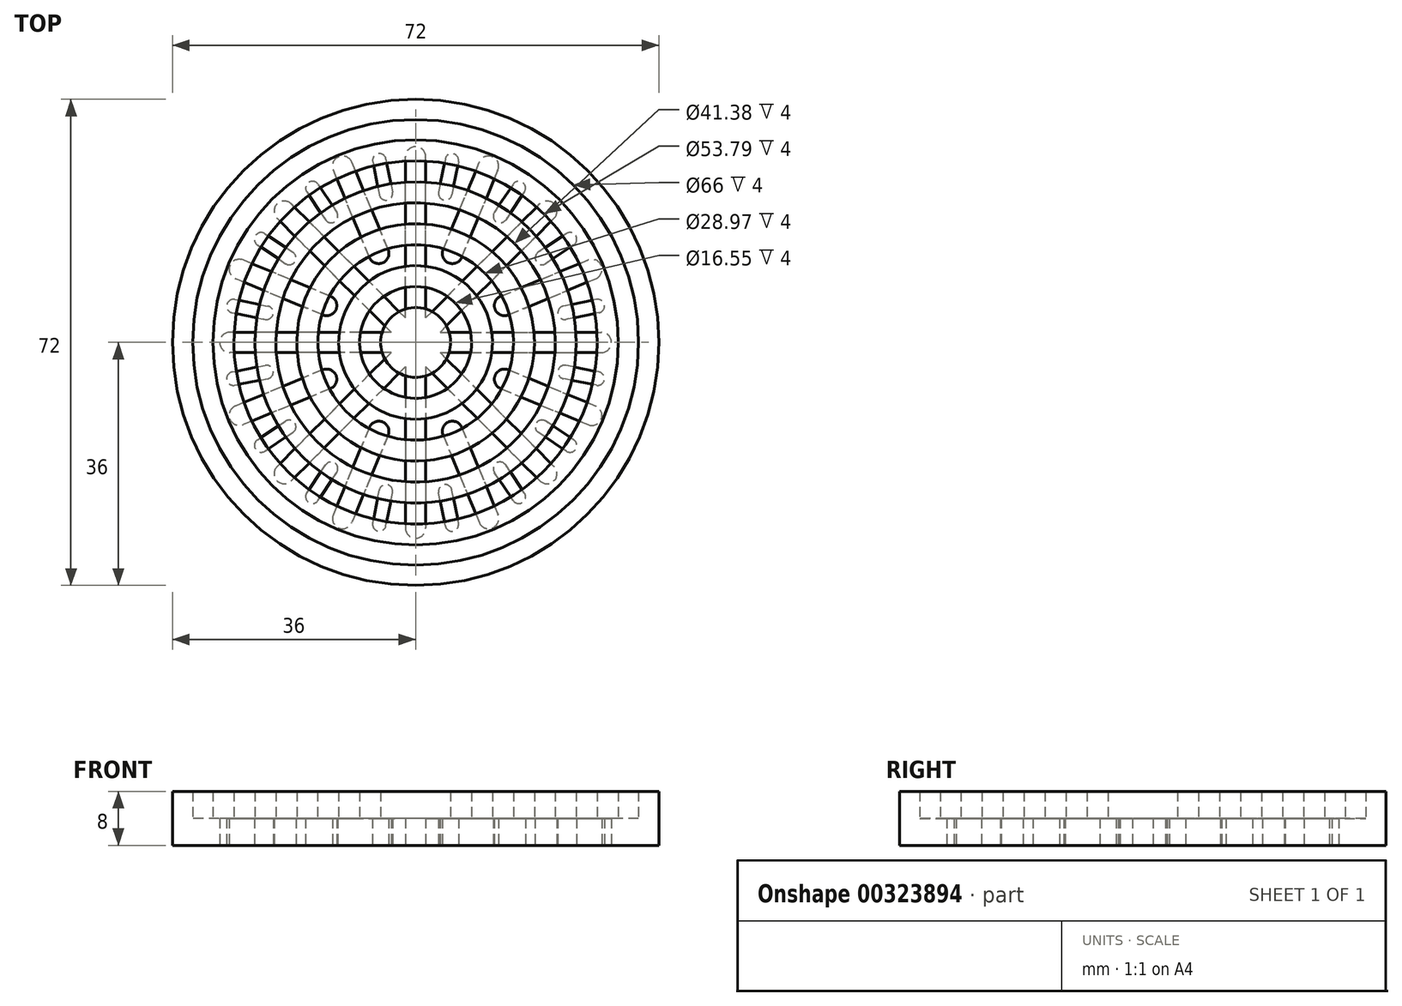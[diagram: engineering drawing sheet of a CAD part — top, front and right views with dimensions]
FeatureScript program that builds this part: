
annotation { "Feature Type Name" : "Feature", "Feature Type Description" : "" }
export const myFeature = defineFeature(function(context is Context, id is Id, definition is map)
    precondition{}
    {
        {
            var Q0;
            Q0=qCreatedBy(makeId("Top.planeOp"),FACE);
            var sketch = newSketch(context, id + "F0", { "sketchPlane" : qUnion([Q0])});
            skCircle(sketch, "E0", {"center": v(0, 0) * mm, "radius": 36 * mm});
            skArc(sketch, "E1.0.endCap", {"start": v(-1.5, 27.5) * mm, "mid": v(0, 29) * mm, "end": v(1.5, 27.5) * mm});
            skArc(sketch, "E2.0.startCap", {"start": v(6.84, 12.6) * mm, "mid": v(4.88, 11.78) * mm, "end": v(4.07, 13.74) * mm});
            skArc(sketch, "E2.0.endCap", {"start": v(9.42, 26.67) * mm, "mid": v(11.38, 27.49) * mm, "end": v(12.2, 25.53) * mm});
            skLineSegment(sketch, "E2.0.left", {"start": v(4.07, 13.74) * mm, "end": v(9.42, 26.67) * mm});
            skLineSegment(sketch, "E2.0.right", {"start": v(6.84, 12.6) * mm, "end": v(12.2, 25.53) * mm});
            skArc(sketch, "E3.0.startCap", {"start": v(4.38, 27.17) * mm, "mid": v(5.56, 27.95) * mm, "end": v(6.35, 26.78) * mm});
            skArc(sketch, "E3.0.endCap", {"start": v(5.37, 21.87) * mm, "mid": v(4.2, 21.09) * mm, "end": v(3.4, 22.26) * mm});
            skLineSegment(sketch, "E3.0.left", {"start": v(6.35, 26.78) * mm, "end": v(5.37, 21.87) * mm});
            skLineSegment(sketch, "E3.0.right", {"start": v(4.38, 27.17) * mm, "end": v(3.4, 22.26) * mm});
            skArc(sketch, "E4.1.0", {"start": v(-20.5, 18.38) * mm, "mid": v(-20.5, 20.5) * mm, "end": v(-18.38, 20.5) * mm});
            skArc(sketch, "E4.2.0", {"start": v(-27.5, -1.5) * mm, "mid": v(-29, 0) * mm, "end": v(-27.5, 1.5) * mm});
            skArc(sketch, "E4.3.0", {"start": v(-18.38, -20.5) * mm, "mid": v(-20.5, -20.5) * mm, "end": v(-20.5, -18.38) * mm});
            skArc(sketch, "E4.4.0", {"start": v(1.5, -27.5) * mm, "mid": v(0, -29) * mm, "end": v(-1.5, -27.5) * mm});
            skArc(sketch, "E4.5.0", {"start": v(20.5, -18.38) * mm, "mid": v(20.5, -20.5) * mm, "end": v(18.38, -20.5) * mm});
            skArc(sketch, "E4.6.0", {"start": v(27.5, 1.5) * mm, "mid": v(29, 0) * mm, "end": v(27.5, -1.5) * mm});
            skArc(sketch, "E4.7.0", {"start": v(18.38, 20.5) * mm, "mid": v(20.5, 20.5) * mm, "end": v(20.5, 18.38) * mm});
            skLineSegment(sketch, "E5.trimOffspring", {"start": v(-1.5, 3.62) * mm, "end": v(-1.5, 27.5) * mm});
            skLineSegment(sketch, "E6.trimOffspring", {"start": v(-3.62, 1.5) * mm, "end": v(-27.5, 1.5) * mm});
            skLineSegment(sketch, "E7.trimOffspring", {"start": v(-1.5, 3.62) * mm, "end": v(-18.38, 20.5) * mm});
            skLineSegment(sketch, "E8.trimOffspring", {"start": v(1.5, 3.62) * mm, "end": v(18.38, 20.5) * mm});
            skLineSegment(sketch, "E9.trimOffspring", {"start": v(1.5, 3.62) * mm, "end": v(1.5, 27.5) * mm});
            skLineSegment(sketch, "E10.trimOffspring", {"start": v(3.62, 1.5) * mm, "end": v(27.5, 1.5) * mm});
            skLineSegment(sketch, "E11.trimOffspring", {"start": v(3.62, 1.5) * mm, "end": v(20.5, 18.38) * mm});
            skLineSegment(sketch, "E12.trimOffspring", {"start": v(3.62, -1.5) * mm, "end": v(20.5, -18.38) * mm});
            skLineSegment(sketch, "E13.trimOffspring", {"start": v(1.5, -3.62) * mm, "end": v(1.5, -27.5) * mm});
            skLineSegment(sketch, "E14.trimOffspring", {"start": v(1.5, -3.62) * mm, "end": v(18.38, -20.5) * mm});
            skLineSegment(sketch, "E15.trimOffspring", {"start": v(-1.5, -3.62) * mm, "end": v(-18.38, -20.5) * mm});
            skLineSegment(sketch, "E16.trimOffspring", {"start": v(-1.5, -3.62) * mm, "end": v(-1.5, -27.5) * mm});
            skLineSegment(sketch, "E17.trimOffspring", {"start": v(-3.62, -1.5) * mm, "end": v(-27.5, -1.5) * mm});
            skLineSegment(sketch, "E18.trimOffspring", {"start": v(-3.62, -1.5) * mm, "end": v(-20.5, -18.38) * mm});
            skLineSegment(sketch, "E19.trimOffspring", {"start": v(-3.62, 1.5) * mm, "end": v(-20.5, 18.38) * mm});
            skLineSegment(sketch, "E20.trimOffspring", {"start": v(3.62, -1.5) * mm, "end": v(27.5, -1.5) * mm});
            skLineSegment(sketch, "E21.1.0", {"start": v(-6.84, 12.6) * mm, "end": v(-12.2, 25.53) * mm});
            skArc(sketch, "E21.1.1", {"start": v(-12.2, 25.53) * mm, "mid": v(-11.38, 27.49) * mm, "end": v(-9.42, 26.67) * mm});
            skLineSegment(sketch, "E21.1.2", {"start": v(-4.07, 13.74) * mm, "end": v(-9.42, 26.67) * mm});
            skArc(sketch, "E21.1.3", {"start": v(-4.07, 13.74) * mm, "mid": v(-4.88, 11.78) * mm, "end": v(-6.84, 12.6) * mm});
            skLineSegment(sketch, "E21.2.0", {"start": v(-13.74, 4.07) * mm, "end": v(-26.67, 9.42) * mm});
            skArc(sketch, "E21.2.1", {"start": v(-26.67, 9.42) * mm, "mid": v(-27.49, 11.38) * mm, "end": v(-25.53, 12.2) * mm});
            skLineSegment(sketch, "E21.2.2", {"start": v(-12.6, 6.84) * mm, "end": v(-25.53, 12.2) * mm});
            skArc(sketch, "E21.2.3", {"start": v(-12.6, 6.84) * mm, "mid": v(-11.78, 4.88) * mm, "end": v(-13.74, 4.07) * mm});
            skLineSegment(sketch, "E21.3.0", {"start": v(-12.6, -6.84) * mm, "end": v(-25.53, -12.2) * mm});
            skArc(sketch, "E21.3.1", {"start": v(-25.53, -12.2) * mm, "mid": v(-27.49, -11.38) * mm, "end": v(-26.67, -9.42) * mm});
            skLineSegment(sketch, "E21.3.2", {"start": v(-13.74, -4.07) * mm, "end": v(-26.67, -9.42) * mm});
            skArc(sketch, "E21.3.3", {"start": v(-13.74, -4.07) * mm, "mid": v(-11.78, -4.88) * mm, "end": v(-12.6, -6.84) * mm});
            skLineSegment(sketch, "E21.4.0", {"start": v(-4.07, -13.74) * mm, "end": v(-9.42, -26.67) * mm});
            skArc(sketch, "E21.4.1", {"start": v(-9.42, -26.67) * mm, "mid": v(-11.38, -27.49) * mm, "end": v(-12.2, -25.53) * mm});
            skLineSegment(sketch, "E21.4.2", {"start": v(-6.84, -12.6) * mm, "end": v(-12.2, -25.53) * mm});
            skArc(sketch, "E21.4.3", {"start": v(-6.84, -12.6) * mm, "mid": v(-4.88, -11.78) * mm, "end": v(-4.07, -13.74) * mm});
            skLineSegment(sketch, "E21.5.0", {"start": v(6.84, -12.6) * mm, "end": v(12.2, -25.53) * mm});
            skArc(sketch, "E21.5.1", {"start": v(12.2, -25.53) * mm, "mid": v(11.38, -27.49) * mm, "end": v(9.42, -26.67) * mm});
            skLineSegment(sketch, "E21.5.2", {"start": v(4.07, -13.74) * mm, "end": v(9.42, -26.67) * mm});
            skArc(sketch, "E21.5.3", {"start": v(4.07, -13.74) * mm, "mid": v(4.88, -11.78) * mm, "end": v(6.84, -12.6) * mm});
            skLineSegment(sketch, "E21.6.0", {"start": v(13.74, -4.07) * mm, "end": v(26.67, -9.42) * mm});
            skArc(sketch, "E21.6.1", {"start": v(26.67, -9.42) * mm, "mid": v(27.49, -11.38) * mm, "end": v(25.53, -12.2) * mm});
            skLineSegment(sketch, "E21.6.2", {"start": v(12.6, -6.84) * mm, "end": v(25.53, -12.2) * mm});
            skArc(sketch, "E21.6.3", {"start": v(12.6, -6.84) * mm, "mid": v(11.78, -4.88) * mm, "end": v(13.74, -4.07) * mm});
            skLineSegment(sketch, "E21.7.0", {"start": v(12.6, 6.84) * mm, "end": v(25.53, 12.2) * mm});
            skArc(sketch, "E21.7.1", {"start": v(25.53, 12.2) * mm, "mid": v(27.49, 11.38) * mm, "end": v(26.67, 9.42) * mm});
            skLineSegment(sketch, "E21.7.2", {"start": v(13.74, 4.07) * mm, "end": v(26.67, 9.42) * mm});
            skArc(sketch, "E21.7.3", {"start": v(13.74, 4.07) * mm, "mid": v(11.78, 4.88) * mm, "end": v(12.6, 6.84) * mm});
            skLineSegment(sketch, "E22.1.0", {"start": v(-6.35, 26.78) * mm, "end": v(-5.37, 21.87) * mm});
            skArc(sketch, "E22.1.1", {"start": v(-6.35, 26.78) * mm, "mid": v(-5.56, 27.95) * mm, "end": v(-4.38, 27.17) * mm});
            skLineSegment(sketch, "E22.1.2", {"start": v(-4.38, 27.17) * mm, "end": v(-3.4, 22.26) * mm});
            skArc(sketch, "E22.1.3", {"start": v(-3.4, 22.26) * mm, "mid": v(-4.2, 21.09) * mm, "end": v(-5.37, 21.87) * mm});
            skLineSegment(sketch, "E22.2.0", {"start": v(-16.1, 22.3) * mm, "end": v(-13.33, 18.15) * mm});
            skArc(sketch, "E22.2.1", {"start": v(-16.1, 22.3) * mm, "mid": v(-15.83, 23.7) * mm, "end": v(-14.45, 23.42) * mm});
            skLineSegment(sketch, "E22.2.2", {"start": v(-14.45, 23.42) * mm, "end": v(-11.67, 19.26) * mm});
            skArc(sketch, "E22.2.3", {"start": v(-11.67, 19.26) * mm, "mid": v(-11.94, 17.88) * mm, "end": v(-13.33, 18.15) * mm});
            skLineSegment(sketch, "E22.3.0", {"start": v(-23.42, 14.45) * mm, "end": v(-19.26, 11.67) * mm});
            skArc(sketch, "E22.3.1", {"start": v(-23.42, 14.45) * mm, "mid": v(-23.7, 15.83) * mm, "end": v(-22.3, 16.1) * mm});
            skLineSegment(sketch, "E22.3.2", {"start": v(-22.3, 16.1) * mm, "end": v(-18.15, 13.33) * mm});
            skArc(sketch, "E22.3.3", {"start": v(-18.15, 13.33) * mm, "mid": v(-17.88, 11.94) * mm, "end": v(-19.26, 11.67) * mm});
            skLineSegment(sketch, "E22.4.0", {"start": v(-27.17, 4.38) * mm, "end": v(-22.26, 3.4) * mm});
            skArc(sketch, "E22.4.1", {"start": v(-27.17, 4.38) * mm, "mid": v(-27.95, 5.56) * mm, "end": v(-26.78, 6.35) * mm});
            skLineSegment(sketch, "E22.4.2", {"start": v(-26.78, 6.35) * mm, "end": v(-21.87, 5.37) * mm});
            skArc(sketch, "E22.4.3", {"start": v(-21.87, 5.37) * mm, "mid": v(-21.09, 4.2) * mm, "end": v(-22.26, 3.4) * mm});
            skLineSegment(sketch, "E22.5.0", {"start": v(-26.78, -6.35) * mm, "end": v(-21.87, -5.37) * mm});
            skArc(sketch, "E22.5.1", {"start": v(-26.78, -6.35) * mm, "mid": v(-27.95, -5.56) * mm, "end": v(-27.17, -4.38) * mm});
            skLineSegment(sketch, "E22.5.2", {"start": v(-27.17, -4.38) * mm, "end": v(-22.26, -3.4) * mm});
            skArc(sketch, "E22.5.3", {"start": v(-22.26, -3.4) * mm, "mid": v(-21.09, -4.2) * mm, "end": v(-21.87, -5.37) * mm});
            skLineSegment(sketch, "E22.6.0", {"start": v(-22.3, -16.1) * mm, "end": v(-18.15, -13.33) * mm});
            skArc(sketch, "E22.6.1", {"start": v(-22.3, -16.1) * mm, "mid": v(-23.7, -15.83) * mm, "end": v(-23.42, -14.45) * mm});
            skLineSegment(sketch, "E22.6.2", {"start": v(-23.42, -14.45) * mm, "end": v(-19.26, -11.67) * mm});
            skArc(sketch, "E22.6.3", {"start": v(-19.26, -11.67) * mm, "mid": v(-17.88, -11.94) * mm, "end": v(-18.15, -13.33) * mm});
            skLineSegment(sketch, "E22.7.0", {"start": v(-14.45, -23.42) * mm, "end": v(-11.67, -19.26) * mm});
            skArc(sketch, "E22.7.1", {"start": v(-14.45, -23.42) * mm, "mid": v(-15.83, -23.7) * mm, "end": v(-16.1, -22.3) * mm});
            skLineSegment(sketch, "E22.7.2", {"start": v(-16.1, -22.3) * mm, "end": v(-13.33, -18.15) * mm});
            skArc(sketch, "E22.7.3", {"start": v(-13.33, -18.15) * mm, "mid": v(-11.94, -17.88) * mm, "end": v(-11.67, -19.26) * mm});
            skLineSegment(sketch, "E22.8.0", {"start": v(-4.38, -27.17) * mm, "end": v(-3.4, -22.26) * mm});
            skArc(sketch, "E22.8.1", {"start": v(-4.38, -27.17) * mm, "mid": v(-5.56, -27.95) * mm, "end": v(-6.35, -26.78) * mm});
            skLineSegment(sketch, "E22.8.2", {"start": v(-6.35, -26.78) * mm, "end": v(-5.37, -21.87) * mm});
            skArc(sketch, "E22.8.3", {"start": v(-5.37, -21.87) * mm, "mid": v(-4.2, -21.09) * mm, "end": v(-3.4, -22.26) * mm});
            skLineSegment(sketch, "E22.9.0", {"start": v(6.35, -26.78) * mm, "end": v(5.37, -21.87) * mm});
            skArc(sketch, "E22.9.1", {"start": v(6.35, -26.78) * mm, "mid": v(5.56, -27.95) * mm, "end": v(4.38, -27.17) * mm});
            skLineSegment(sketch, "E22.9.2", {"start": v(4.38, -27.17) * mm, "end": v(3.4, -22.26) * mm});
            skArc(sketch, "E22.9.3", {"start": v(3.4, -22.26) * mm, "mid": v(4.2, -21.09) * mm, "end": v(5.37, -21.87) * mm});
            skLineSegment(sketch, "E22.10.0", {"start": v(16.1, -22.3) * mm, "end": v(13.33, -18.15) * mm});
            skArc(sketch, "E22.10.1", {"start": v(16.1, -22.3) * mm, "mid": v(15.83, -23.7) * mm, "end": v(14.45, -23.42) * mm});
            skLineSegment(sketch, "E22.10.2", {"start": v(14.45, -23.42) * mm, "end": v(11.67, -19.26) * mm});
            skArc(sketch, "E22.10.3", {"start": v(11.67, -19.26) * mm, "mid": v(11.94, -17.88) * mm, "end": v(13.33, -18.15) * mm});
            skLineSegment(sketch, "E22.11.0", {"start": v(23.42, -14.45) * mm, "end": v(19.26, -11.67) * mm});
            skArc(sketch, "E22.11.1", {"start": v(23.42, -14.45) * mm, "mid": v(23.7, -15.83) * mm, "end": v(22.3, -16.1) * mm});
            skLineSegment(sketch, "E22.11.2", {"start": v(22.3, -16.1) * mm, "end": v(18.15, -13.33) * mm});
            skArc(sketch, "E22.11.3", {"start": v(18.15, -13.33) * mm, "mid": v(17.88, -11.94) * mm, "end": v(19.26, -11.67) * mm});
            skLineSegment(sketch, "E22.12.0", {"start": v(27.17, -4.38) * mm, "end": v(22.26, -3.4) * mm});
            skArc(sketch, "E22.12.1", {"start": v(27.17, -4.38) * mm, "mid": v(27.95, -5.56) * mm, "end": v(26.78, -6.35) * mm});
            skLineSegment(sketch, "E22.12.2", {"start": v(26.78, -6.35) * mm, "end": v(21.87, -5.37) * mm});
            skArc(sketch, "E22.12.3", {"start": v(21.87, -5.37) * mm, "mid": v(21.09, -4.2) * mm, "end": v(22.26, -3.4) * mm});
            skLineSegment(sketch, "E22.13.0", {"start": v(26.78, 6.35) * mm, "end": v(21.87, 5.37) * mm});
            skArc(sketch, "E22.13.1", {"start": v(26.78, 6.35) * mm, "mid": v(27.95, 5.56) * mm, "end": v(27.17, 4.38) * mm});
            skLineSegment(sketch, "E22.13.2", {"start": v(27.17, 4.38) * mm, "end": v(22.26, 3.4) * mm});
            skArc(sketch, "E22.13.3", {"start": v(22.26, 3.4) * mm, "mid": v(21.09, 4.2) * mm, "end": v(21.87, 5.37) * mm});
            skLineSegment(sketch, "E22.14.0", {"start": v(22.3, 16.1) * mm, "end": v(18.15, 13.33) * mm});
            skArc(sketch, "E22.14.1", {"start": v(22.3, 16.1) * mm, "mid": v(23.7, 15.83) * mm, "end": v(23.42, 14.45) * mm});
            skLineSegment(sketch, "E22.14.2", {"start": v(23.42, 14.45) * mm, "end": v(19.26, 11.67) * mm});
            skArc(sketch, "E22.14.3", {"start": v(19.26, 11.67) * mm, "mid": v(17.88, 11.94) * mm, "end": v(18.15, 13.33) * mm});
            skLineSegment(sketch, "E22.15.0", {"start": v(14.45, 23.42) * mm, "end": v(11.67, 19.26) * mm});
            skArc(sketch, "E22.15.1", {"start": v(14.45, 23.42) * mm, "mid": v(15.83, 23.7) * mm, "end": v(16.1, 22.3) * mm});
            skLineSegment(sketch, "E22.15.2", {"start": v(16.1, 22.3) * mm, "end": v(13.33, 18.15) * mm});
            skArc(sketch, "E22.15.3", {"start": v(13.33, 18.15) * mm, "mid": v(11.94, 17.88) * mm, "end": v(11.67, 19.26) * mm});
            skSolve(sketch);
        }
        {
            var Q0;
            Q0 = qSketchRegion(id + "F0", true);
            extrude(context, id + "F1", {"entities" : qUnion([Q0]), "depth" : 4 * mm});
        }
        {
            var Q0;
            Q0=makeQuery(id+"F1.opExtrude","CAP_FACE",FACE,{"disambiguationData":[OSD([sQuery(id+"F0.wireOp",EDGE,"E0"),sQuery(id+"F0.wireOp",EDGE,"E1.0.endCap"),sQuery(id+"F0.wireOp",EDGE,"E2.0.startCap"),sQuery(id+"F0.wireOp",EDGE,"E2.0.endCap"),sQuery(id+"F0.wireOp",EDGE,"E2.0.left"),sQuery(id+"F0.wireOp",EDGE,"E2.0.right"),sQuery(id+"F0.wireOp",EDGE,"E3.0.startCap"),sQuery(id+"F0.wireOp",EDGE,"E3.0.endCap"),sQuery(id+"F0.wireOp",EDGE,"E3.0.left"),sQuery(id+"F0.wireOp",EDGE,"E3.0.right"),sQuery(id+"F0.wireOp",EDGE,"E4.1.0"),sQuery(id+"F0.wireOp",EDGE,"E4.2.0"),sQuery(id+"F0.wireOp",EDGE,"E4.3.0"),sQuery(id+"F0.wireOp",EDGE,"E4.4.0"),sQuery(id+"F0.wireOp",EDGE,"E4.5.0"),sQuery(id+"F0.wireOp",EDGE,"E4.6.0"),sQuery(id+"F0.wireOp",EDGE,"E4.7.0"),sQuery(id+"F0.wireOp",EDGE,"E5.trimOffspring"),sQuery(id+"F0.wireOp",EDGE,"E6.trimOffspring"),sQuery(id+"F0.wireOp",EDGE,"E7.trimOffspring"),sQuery(id+"F0.wireOp",EDGE,"E8.trimOffspring"),sQuery(id+"F0.wireOp",EDGE,"E9.trimOffspring"),sQuery(id+"F0.wireOp",EDGE,"E10.trimOffspring"),sQuery(id+"F0.wireOp",EDGE,"E11.trimOffspring"),sQuery(id+"F0.wireOp",EDGE,"E12.trimOffspring"),sQuery(id+"F0.wireOp",EDGE,"E13.trimOffspring"),sQuery(id+"F0.wireOp",EDGE,"E14.trimOffspring"),sQuery(id+"F0.wireOp",EDGE,"E15.trimOffspring"),sQuery(id+"F0.wireOp",EDGE,"E16.trimOffspring"),sQuery(id+"F0.wireOp",EDGE,"E17.trimOffspring"),sQuery(id+"F0.wireOp",EDGE,"E18.trimOffspring"),sQuery(id+"F0.wireOp",EDGE,"E19.trimOffspring"),sQuery(id+"F0.wireOp",EDGE,"E20.trimOffspring"),sQuery(id+"F0.wireOp",EDGE,"E21.1.0"),sQuery(id+"F0.wireOp",EDGE,"E21.1.1"),sQuery(id+"F0.wireOp",EDGE,"E21.1.2"),sQuery(id+"F0.wireOp",EDGE,"E21.1.3"),sQuery(id+"F0.wireOp",EDGE,"E21.2.0"),sQuery(id+"F0.wireOp",EDGE,"E21.2.1"),sQuery(id+"F0.wireOp",EDGE,"E21.2.2"),sQuery(id+"F0.wireOp",EDGE,"E21.2.3"),sQuery(id+"F0.wireOp",EDGE,"E21.3.0"),sQuery(id+"F0.wireOp",EDGE,"E21.3.1"),sQuery(id+"F0.wireOp",EDGE,"E21.3.2"),sQuery(id+"F0.wireOp",EDGE,"E21.3.3"),sQuery(id+"F0.wireOp",EDGE,"E21.4.0"),sQuery(id+"F0.wireOp",EDGE,"E21.4.1"),sQuery(id+"F0.wireOp",EDGE,"E21.4.2"),sQuery(id+"F0.wireOp",EDGE,"E21.4.3"),sQuery(id+"F0.wireOp",EDGE,"E21.5.0"),sQuery(id+"F0.wireOp",EDGE,"E21.5.1"),sQuery(id+"F0.wireOp",EDGE,"E21.5.2"),sQuery(id+"F0.wireOp",EDGE,"E21.5.3"),sQuery(id+"F0.wireOp",EDGE,"E21.6.0"),sQuery(id+"F0.wireOp",EDGE,"E21.6.1"),sQuery(id+"F0.wireOp",EDGE,"E21.6.2"),sQuery(id+"F0.wireOp",EDGE,"E21.6.3"),sQuery(id+"F0.wireOp",EDGE,"E21.7.0"),sQuery(id+"F0.wireOp",EDGE,"E21.7.1"),sQuery(id+"F0.wireOp",EDGE,"E21.7.2"),sQuery(id+"F0.wireOp",EDGE,"E21.7.3"),sQuery(id+"F0.wireOp",EDGE,"E22.1.0"),sQuery(id+"F0.wireOp",EDGE,"E22.1.1"),sQuery(id+"F0.wireOp",EDGE,"E22.1.2"),sQuery(id+"F0.wireOp",EDGE,"E22.1.3"),sQuery(id+"F0.wireOp",EDGE,"E22.2.0"),sQuery(id+"F0.wireOp",EDGE,"E22.2.1"),sQuery(id+"F0.wireOp",EDGE,"E22.2.2"),sQuery(id+"F0.wireOp",EDGE,"E22.2.3"),sQuery(id+"F0.wireOp",EDGE,"E22.3.0"),sQuery(id+"F0.wireOp",EDGE,"E22.3.1"),sQuery(id+"F0.wireOp",EDGE,"E22.3.2"),sQuery(id+"F0.wireOp",EDGE,"E22.3.3"),sQuery(id+"F0.wireOp",EDGE,"E22.4.0"),sQuery(id+"F0.wireOp",EDGE,"E22.4.1"),sQuery(id+"F0.wireOp",EDGE,"E22.4.2"),sQuery(id+"F0.wireOp",EDGE,"E22.4.3"),sQuery(id+"F0.wireOp",EDGE,"E22.5.0"),sQuery(id+"F0.wireOp",EDGE,"E22.5.1"),sQuery(id+"F0.wireOp",EDGE,"E22.5.2"),sQuery(id+"F0.wireOp",EDGE,"E22.5.3"),sQuery(id+"F0.wireOp",EDGE,"E22.6.0"),sQuery(id+"F0.wireOp",EDGE,"E22.6.1"),sQuery(id+"F0.wireOp",EDGE,"E22.6.2"),sQuery(id+"F0.wireOp",EDGE,"E22.6.3"),sQuery(id+"F0.wireOp",EDGE,"E22.7.0"),sQuery(id+"F0.wireOp",EDGE,"E22.7.1"),sQuery(id+"F0.wireOp",EDGE,"E22.7.2"),sQuery(id+"F0.wireOp",EDGE,"E22.7.3"),sQuery(id+"F0.wireOp",EDGE,"E22.8.0"),sQuery(id+"F0.wireOp",EDGE,"E22.8.1"),sQuery(id+"F0.wireOp",EDGE,"E22.8.2"),sQuery(id+"F0.wireOp",EDGE,"E22.8.3"),sQuery(id+"F0.wireOp",EDGE,"E22.9.0"),sQuery(id+"F0.wireOp",EDGE,"E22.9.1"),sQuery(id+"F0.wireOp",EDGE,"E22.9.2"),sQuery(id+"F0.wireOp",EDGE,"E22.9.3"),sQuery(id+"F0.wireOp",EDGE,"E22.10.0"),sQuery(id+"F0.wireOp",EDGE,"E22.10.1"),sQuery(id+"F0.wireOp",EDGE,"E22.10.2"),sQuery(id+"F0.wireOp",EDGE,"E22.10.3"),sQuery(id+"F0.wireOp",EDGE,"E22.11.0"),sQuery(id+"F0.wireOp",EDGE,"E22.11.1"),sQuery(id+"F0.wireOp",EDGE,"E22.11.2"),sQuery(id+"F0.wireOp",EDGE,"E22.11.3"),sQuery(id+"F0.wireOp",EDGE,"E22.12.0"),sQuery(id+"F0.wireOp",EDGE,"E22.12.1"),sQuery(id+"F0.wireOp",EDGE,"E22.12.2"),sQuery(id+"F0.wireOp",EDGE,"E22.12.3"),sQuery(id+"F0.wireOp",EDGE,"E22.13.0"),sQuery(id+"F0.wireOp",EDGE,"E22.13.1"),sQuery(id+"F0.wireOp",EDGE,"E22.13.2"),sQuery(id+"F0.wireOp",EDGE,"E22.13.3"),sQuery(id+"F0.wireOp",EDGE,"E22.14.0"),sQuery(id+"F0.wireOp",EDGE,"E22.14.1"),sQuery(id+"F0.wireOp",EDGE,"E22.14.2"),sQuery(id+"F0.wireOp",EDGE,"E22.14.3"),sQuery(id+"F0.wireOp",EDGE,"E22.15.0"),sQuery(id+"F0.wireOp",EDGE,"E22.15.1"),sQuery(id+"F0.wireOp",EDGE,"E22.15.2"),sQuery(id+"F0.wireOp",EDGE,"E22.15.3")])],"isStart":false});
            var sketch = newSketch(context, id + "F2", { "sketchPlane" : qUnion([Q0])});
            skCircle(sketch, "E23", {"center": v(0, 0) * mm, "radius": 23.8 * mm});
            skCircle(sketch, "E24", {"center": v(0, 0) * mm, "radius": 26.9 * mm});
            skCircle(sketch, "E25", {"center": v(0, 0) * mm, "radius": 30 * mm});
            skCircle(sketch, "E26", {"center": v(0, 0) * mm, "radius": 33 * mm});
            skCircle(sketch, "E27", {"center": v(0, 0) * mm, "radius": 20.69 * mm});
            skCircle(sketch, "E28", {"center": v(0, 0) * mm, "radius": 17.59 * mm});
            skCircle(sketch, "E29", {"center": v(0, 0) * mm, "radius": 14.48 * mm});
            skCircle(sketch, "E30", {"center": v(0, 0) * mm, "radius": 11.38 * mm});
            skCircle(sketch, "E31", {"center": v(0, 0) * mm, "radius": 8.28 * mm});
            skCircle(sketch, "E32", {"center": v(0, 0) * mm, "radius": 5.17 * mm});
            skSolve(sketch);
        }
        {
            var Q0;
            {var subQ0=sQuery(id+"F2.wireOp",EDGE,"E32");var subQ1=makeQuery(id+"F1.opExtrude","CAP_EDGE",EDGE,{"disambiguationData":[OSD([sQuery(id+"F0.wireOp",EDGE,"E8.trimOffspring")])],"isStart":false});var subQ2=makeQuery(id+"F2.imprint","INTERSECT",VERTEX,{"derivedFrom":[subQ1,subQ0]});Q0=makeQuery(id+"F2.imprint","IMPRINT",FACE,{"disambiguationData":[TD([[makeQuery(id+"F2.imprint","IMPRINT",EDGE,{"disambiguationData":[TD([[subQ2,-1.0]])],"derivedFrom":subQ0}),1.0]])]});}
            var Q1;
            {var subQ0=sQuery(id+"F2.wireOp",EDGE,"E32");var subQ1=makeQuery(id+"F1.opExtrude","CAP_EDGE",EDGE,{"disambiguationData":[OSD([sQuery(id+"F0.wireOp",EDGE,"E11.trimOffspring")])],"isStart":false});var subQ2=makeQuery(id+"F2.imprint","INTERSECT",VERTEX,{"derivedFrom":[subQ1,subQ0]});Q1=makeQuery(id+"F2.imprint","IMPRINT",FACE,{"disambiguationData":[TD([[makeQuery(id+"F2.imprint","IMPRINT",EDGE,{"disambiguationData":[TD([[subQ2,1.0]])],"derivedFrom":subQ0}),1.0]])]});}
            var Q2;
            {var subQ0=sQuery(id+"F2.wireOp",EDGE,"E32");var subQ1=makeQuery(id+"F1.opExtrude","CAP_EDGE",EDGE,{"disambiguationData":[OSD([sQuery(id+"F0.wireOp",EDGE,"E12.trimOffspring")])],"isStart":false});var subQ2=makeQuery(id+"F2.imprint","INTERSECT",VERTEX,{"derivedFrom":[subQ1,subQ0]});Q2=makeQuery(id+"F2.imprint","IMPRINT",FACE,{"disambiguationData":[TD([[makeQuery(id+"F2.imprint","IMPRINT",EDGE,{"disambiguationData":[TD([[subQ2,-1.0]])],"derivedFrom":subQ0}),1.0]])]});}
            var Q3;
            {var subQ0=sQuery(id+"F2.wireOp",EDGE,"E32");var subQ1=makeQuery(id+"F1.opExtrude","CAP_EDGE",EDGE,{"disambiguationData":[OSD([sQuery(id+"F0.wireOp",EDGE,"E13.trimOffspring")])],"isStart":false});var subQ2=makeQuery(id+"F2.imprint","INTERSECT",VERTEX,{"derivedFrom":[subQ1,subQ0]});Q3=makeQuery(id+"F2.imprint","IMPRINT",FACE,{"disambiguationData":[TD([[makeQuery(id+"F2.imprint","IMPRINT",EDGE,{"disambiguationData":[TD([[subQ2,-1.0]])],"derivedFrom":subQ0}),1.0]])]});}
            var Q4;
            {var subQ0=sQuery(id+"F2.wireOp",EDGE,"E32");var subQ1=makeQuery(id+"F1.opExtrude","CAP_EDGE",EDGE,{"disambiguationData":[OSD([sQuery(id+"F0.wireOp",EDGE,"E15.trimOffspring")])],"isStart":false});var subQ2=makeQuery(id+"F2.imprint","INTERSECT",VERTEX,{"derivedFrom":[subQ1,subQ0]});Q4=makeQuery(id+"F2.imprint","IMPRINT",FACE,{"disambiguationData":[TD([[makeQuery(id+"F2.imprint","IMPRINT",EDGE,{"disambiguationData":[TD([[subQ2,-1.0]])],"derivedFrom":subQ0}),1.0]])]});}
            var Q5;
            {var subQ0=sQuery(id+"F2.wireOp",EDGE,"E32");var subQ1=makeQuery(id+"F1.opExtrude","CAP_EDGE",EDGE,{"disambiguationData":[OSD([sQuery(id+"F0.wireOp",EDGE,"E17.trimOffspring")])],"isStart":false});var subQ2=makeQuery(id+"F2.imprint","INTERSECT",VERTEX,{"derivedFrom":[subQ1,subQ0]});Q5=makeQuery(id+"F2.imprint","IMPRINT",FACE,{"disambiguationData":[TD([[makeQuery(id+"F2.imprint","IMPRINT",EDGE,{"disambiguationData":[TD([[subQ2,-1.0]])],"derivedFrom":subQ0}),1.0]])]});}
            var Q6;
            {var subQ0=sQuery(id+"F2.wireOp",EDGE,"E32");var subQ1=makeQuery(id+"F1.opExtrude","CAP_EDGE",EDGE,{"disambiguationData":[OSD([sQuery(id+"F0.wireOp",EDGE,"E19.trimOffspring")])],"isStart":false});var subQ2=makeQuery(id+"F2.imprint","INTERSECT",VERTEX,{"derivedFrom":[subQ1,subQ0]});Q6=makeQuery(id+"F2.imprint","IMPRINT",FACE,{"disambiguationData":[TD([[makeQuery(id+"F2.imprint","IMPRINT",EDGE,{"disambiguationData":[TD([[subQ2,-1.0]])],"derivedFrom":subQ0}),1.0]])]});}
            var Q7;
            {var subQ0=sQuery(id+"F2.wireOp",EDGE,"E32");var subQ1=makeQuery(id+"F1.opExtrude","CAP_EDGE",EDGE,{"disambiguationData":[OSD([sQuery(id+"F0.wireOp",EDGE,"E5.trimOffspring")])],"isStart":false});var subQ2=makeQuery(id+"F2.imprint","INTERSECT",VERTEX,{"derivedFrom":[subQ1,subQ0]});Q7=makeQuery(id+"F2.imprint","IMPRINT",FACE,{"disambiguationData":[TD([[makeQuery(id+"F2.imprint","IMPRINT",EDGE,{"disambiguationData":[TD([[subQ2,-1.0]])],"derivedFrom":subQ0}),1.0]])]});}
            var Q8;
            {var subQ0=makeQuery(id+"F1.opExtrude","CAP_EDGE",EDGE,{"disambiguationData":[OSD([sQuery(id+"F0.wireOp",EDGE,"E11.trimOffspring")])],"isStart":false});var subQ3=sQuery(id+"F2.wireOp",EDGE,"E32");var subQ34=makeQuery(id+"F2.imprint","INTERSECT",VERTEX,{"derivedFrom":[subQ0,subQ3]});Q8=makeQuery(id+"F2.imprint","IMPRINT",FACE,{"disambiguationData":[TD([[makeQuery(id+"F2.imprint","IMPRINT",EDGE,{"disambiguationData":[TD([[subQ34,-1.0]])],"derivedFrom":subQ3}),1.0]])]});}
            var Q9;
            {var subQ0=sQuery(id+"F2.wireOp",EDGE,"E30");var subQ1=makeQuery(id+"F1.opExtrude","CAP_EDGE",EDGE,{"disambiguationData":[OSD([sQuery(id+"F0.wireOp",EDGE,"E11.trimOffspring")])],"isStart":false});var subQ2=makeQuery(id+"F2.imprint","INTERSECT",VERTEX,{"derivedFrom":[subQ1,subQ0]});Q9=makeQuery(id+"F2.imprint","IMPRINT",FACE,{"disambiguationData":[TD([[makeQuery(id+"F2.imprint","IMPRINT",EDGE,{"disambiguationData":[TD([[subQ2,1.0]])],"derivedFrom":subQ0}),1.0]])]});}
            var Q10;
            {var subQ0=sQuery(id+"F2.wireOp",EDGE,"E30");var subQ1=makeQuery(id+"F1.opExtrude","CAP_EDGE",EDGE,{"disambiguationData":[OSD([sQuery(id+"F0.wireOp",EDGE,"E10.trimOffspring")])],"isStart":false});var subQ2=makeQuery(id+"F2.imprint","INTERSECT",VERTEX,{"derivedFrom":[subQ1,subQ0]});Q10=makeQuery(id+"F2.imprint","IMPRINT",FACE,{"disambiguationData":[TD([[makeQuery(id+"F2.imprint","IMPRINT",EDGE,{"disambiguationData":[TD([[subQ2,1.0]])],"derivedFrom":subQ0}),1.0]])]});}
            var Q11;
            {var subQ0=sQuery(id+"F2.wireOp",EDGE,"E30");var subQ1=makeQuery(id+"F1.opExtrude","CAP_EDGE",EDGE,{"disambiguationData":[OSD([sQuery(id+"F0.wireOp",EDGE,"E12.trimOffspring")])],"isStart":false});var subQ2=makeQuery(id+"F2.imprint","INTERSECT",VERTEX,{"derivedFrom":[subQ1,subQ0]});Q11=makeQuery(id+"F2.imprint","IMPRINT",FACE,{"disambiguationData":[TD([[makeQuery(id+"F2.imprint","IMPRINT",EDGE,{"disambiguationData":[TD([[subQ2,-1.0]])],"derivedFrom":subQ0}),1.0]])]});}
            var Q12;
            {var subQ0=sQuery(id+"F2.wireOp",EDGE,"E30");var subQ1=makeQuery(id+"F1.opExtrude","CAP_EDGE",EDGE,{"disambiguationData":[OSD([sQuery(id+"F0.wireOp",EDGE,"E14.trimOffspring")])],"isStart":false});var subQ2=makeQuery(id+"F2.imprint","INTERSECT",VERTEX,{"derivedFrom":[subQ1,subQ0]});Q12=makeQuery(id+"F2.imprint","IMPRINT",FACE,{"disambiguationData":[TD([[makeQuery(id+"F2.imprint","IMPRINT",EDGE,{"disambiguationData":[TD([[subQ2,-1.0]])],"derivedFrom":subQ0}),1.0]])]});}
            var Q13;
            {var subQ0=sQuery(id+"F2.wireOp",EDGE,"E30");var subQ1=makeQuery(id+"F1.opExtrude","CAP_EDGE",EDGE,{"disambiguationData":[OSD([sQuery(id+"F0.wireOp",EDGE,"E13.trimOffspring")])],"isStart":false});var subQ2=makeQuery(id+"F2.imprint","INTERSECT",VERTEX,{"derivedFrom":[subQ1,subQ0]});Q13=makeQuery(id+"F2.imprint","IMPRINT",FACE,{"disambiguationData":[TD([[makeQuery(id+"F2.imprint","IMPRINT",EDGE,{"disambiguationData":[TD([[subQ2,-1.0]])],"derivedFrom":subQ0}),1.0]])]});}
            var Q14;
            {var subQ0=sQuery(id+"F2.wireOp",EDGE,"E30");var subQ1=makeQuery(id+"F1.opExtrude","CAP_EDGE",EDGE,{"disambiguationData":[OSD([sQuery(id+"F0.wireOp",EDGE,"E16.trimOffspring")])],"isStart":false});var subQ2=makeQuery(id+"F2.imprint","INTERSECT",VERTEX,{"derivedFrom":[subQ1,subQ0]});Q14=makeQuery(id+"F2.imprint","IMPRINT",FACE,{"disambiguationData":[TD([[makeQuery(id+"F2.imprint","IMPRINT",EDGE,{"disambiguationData":[TD([[subQ2,-1.0]])],"derivedFrom":subQ0}),1.0]])]});}
            var Q15;
            {var subQ0=sQuery(id+"F2.wireOp",EDGE,"E30");var subQ1=makeQuery(id+"F1.opExtrude","CAP_EDGE",EDGE,{"disambiguationData":[OSD([sQuery(id+"F0.wireOp",EDGE,"E15.trimOffspring")])],"isStart":false});var subQ2=makeQuery(id+"F2.imprint","INTERSECT",VERTEX,{"derivedFrom":[subQ1,subQ0]});Q15=makeQuery(id+"F2.imprint","IMPRINT",FACE,{"disambiguationData":[TD([[makeQuery(id+"F2.imprint","IMPRINT",EDGE,{"disambiguationData":[TD([[subQ2,-1.0]])],"derivedFrom":subQ0}),1.0]])]});}
            var Q16;
            {var subQ0=sQuery(id+"F2.wireOp",EDGE,"E30");var subQ1=makeQuery(id+"F1.opExtrude","CAP_EDGE",EDGE,{"disambiguationData":[OSD([sQuery(id+"F0.wireOp",EDGE,"E18.trimOffspring")])],"isStart":false});var subQ2=makeQuery(id+"F2.imprint","INTERSECT",VERTEX,{"derivedFrom":[subQ1,subQ0]});Q16=makeQuery(id+"F2.imprint","IMPRINT",FACE,{"disambiguationData":[TD([[makeQuery(id+"F2.imprint","IMPRINT",EDGE,{"disambiguationData":[TD([[subQ2,-1.0]])],"derivedFrom":subQ0}),1.0]])]});}
            var Q17;
            {var subQ0=sQuery(id+"F2.wireOp",EDGE,"E30");var subQ1=makeQuery(id+"F1.opExtrude","CAP_EDGE",EDGE,{"disambiguationData":[OSD([sQuery(id+"F0.wireOp",EDGE,"E17.trimOffspring")])],"isStart":false});var subQ2=makeQuery(id+"F2.imprint","INTERSECT",VERTEX,{"derivedFrom":[subQ1,subQ0]});Q17=makeQuery(id+"F2.imprint","IMPRINT",FACE,{"disambiguationData":[TD([[makeQuery(id+"F2.imprint","IMPRINT",EDGE,{"disambiguationData":[TD([[subQ2,-1.0]])],"derivedFrom":subQ0}),1.0]])]});}
            var Q18;
            {var subQ0=sQuery(id+"F2.wireOp",EDGE,"E30");var subQ1=makeQuery(id+"F1.opExtrude","CAP_EDGE",EDGE,{"disambiguationData":[OSD([sQuery(id+"F0.wireOp",EDGE,"E6.trimOffspring")])],"isStart":false});var subQ2=makeQuery(id+"F2.imprint","INTERSECT",VERTEX,{"derivedFrom":[subQ1,subQ0]});Q18=makeQuery(id+"F2.imprint","IMPRINT",FACE,{"disambiguationData":[TD([[makeQuery(id+"F2.imprint","IMPRINT",EDGE,{"disambiguationData":[TD([[subQ2,-1.0]])],"derivedFrom":subQ0}),1.0]])]});}
            var Q19;
            {var subQ0=sQuery(id+"F2.wireOp",EDGE,"E30");var subQ1=makeQuery(id+"F1.opExtrude","CAP_EDGE",EDGE,{"disambiguationData":[OSD([sQuery(id+"F0.wireOp",EDGE,"E19.trimOffspring")])],"isStart":false});var subQ2=makeQuery(id+"F2.imprint","INTERSECT",VERTEX,{"derivedFrom":[subQ1,subQ0]});Q19=makeQuery(id+"F2.imprint","IMPRINT",FACE,{"disambiguationData":[TD([[makeQuery(id+"F2.imprint","IMPRINT",EDGE,{"disambiguationData":[TD([[subQ2,-1.0]])],"derivedFrom":subQ0}),1.0]])]});}
            var Q20;
            {var subQ0=sQuery(id+"F2.wireOp",EDGE,"E30");var subQ1=makeQuery(id+"F1.opExtrude","CAP_EDGE",EDGE,{"disambiguationData":[OSD([sQuery(id+"F0.wireOp",EDGE,"E7.trimOffspring")])],"isStart":false});var subQ2=makeQuery(id+"F2.imprint","INTERSECT",VERTEX,{"derivedFrom":[subQ1,subQ0]});Q20=makeQuery(id+"F2.imprint","IMPRINT",FACE,{"disambiguationData":[TD([[makeQuery(id+"F2.imprint","IMPRINT",EDGE,{"disambiguationData":[TD([[subQ2,-1.0]])],"derivedFrom":subQ0}),1.0]])]});}
            var Q21;
            {var subQ0=sQuery(id+"F2.wireOp",EDGE,"E30");var subQ1=makeQuery(id+"F1.opExtrude","CAP_EDGE",EDGE,{"disambiguationData":[OSD([sQuery(id+"F0.wireOp",EDGE,"E5.trimOffspring")])],"isStart":false});var subQ2=makeQuery(id+"F2.imprint","INTERSECT",VERTEX,{"derivedFrom":[subQ1,subQ0]});Q21=makeQuery(id+"F2.imprint","IMPRINT",FACE,{"disambiguationData":[TD([[makeQuery(id+"F2.imprint","IMPRINT",EDGE,{"disambiguationData":[TD([[subQ2,-1.0]])],"derivedFrom":subQ0}),1.0]])]});}
            var Q22;
            {var subQ0=sQuery(id+"F2.wireOp",EDGE,"E30");var subQ1=makeQuery(id+"F1.opExtrude","CAP_EDGE",EDGE,{"disambiguationData":[OSD([sQuery(id+"F0.wireOp",EDGE,"E9.trimOffspring")])],"isStart":false});var subQ2=makeQuery(id+"F2.imprint","INTERSECT",VERTEX,{"derivedFrom":[subQ1,subQ0]});Q22=makeQuery(id+"F2.imprint","IMPRINT",FACE,{"disambiguationData":[TD([[makeQuery(id+"F2.imprint","IMPRINT",EDGE,{"disambiguationData":[TD([[subQ2,-1.0]])],"derivedFrom":subQ0}),1.0]])]});}
            var Q23;
            {var subQ0=sQuery(id+"F2.wireOp",EDGE,"E30");var subQ1=makeQuery(id+"F1.opExtrude","CAP_EDGE",EDGE,{"disambiguationData":[OSD([sQuery(id+"F0.wireOp",EDGE,"E8.trimOffspring")])],"isStart":false});var subQ2=makeQuery(id+"F2.imprint","INTERSECT",VERTEX,{"derivedFrom":[subQ1,subQ0]});Q23=makeQuery(id+"F2.imprint","IMPRINT",FACE,{"disambiguationData":[TD([[makeQuery(id+"F2.imprint","IMPRINT",EDGE,{"disambiguationData":[TD([[subQ2,-1.0]])],"derivedFrom":subQ0}),1.0]])]});}
            var Q24;
            {var subQ0=sQuery(id+"F2.wireOp",EDGE,"E30");var subQ1=makeQuery(id+"F1.opExtrude","CAP_EDGE",EDGE,{"disambiguationData":[OSD([sQuery(id+"F0.wireOp",EDGE,"E11.trimOffspring")])],"isStart":false});var subQ2=makeQuery(id+"F2.imprint","INTERSECT",VERTEX,{"derivedFrom":[subQ1,subQ0]});Q24=makeQuery(id+"F2.imprint","IMPRINT",FACE,{"disambiguationData":[TD([[makeQuery(id+"F2.imprint","IMPRINT",EDGE,{"disambiguationData":[TD([[subQ2,-1.0]])],"derivedFrom":subQ0}),1.0]])]});}
            var Q25;
            {var subQ1=makeQuery(id+"F1.opExtrude","CAP_EDGE",EDGE,{"disambiguationData":[OSD([sQuery(id+"F0.wireOp",EDGE,"E21.7.2")])],"isStart":false});var subQ3=sQuery(id+"F2.wireOp",EDGE,"E28");var subQ4=makeQuery(id+"F2.imprint","INTERSECT",VERTEX,{"derivedFrom":[subQ1,subQ3]});Q25=makeQuery(id+"F2.imprint","IMPRINT",FACE,{"disambiguationData":[TD([[makeQuery(id+"F2.imprint","IMPRINT",EDGE,{"disambiguationData":[TD([[subQ4,-1.0]])],"derivedFrom":subQ3}),1.0]])]});}
            var Q26;
            {var subQ1=makeQuery(id+"F1.opExtrude","CAP_EDGE",EDGE,{"disambiguationData":[OSD([sQuery(id+"F0.wireOp",EDGE,"E21.7.2")])],"isStart":false});var subQ5=sQuery(id+"F2.wireOp",EDGE,"E28");var subQ6=makeQuery(id+"F2.imprint","INTERSECT",VERTEX,{"derivedFrom":[subQ1,subQ5]});Q26=makeQuery(id+"F2.imprint","IMPRINT",FACE,{"disambiguationData":[TD([[makeQuery(id+"F2.imprint","IMPRINT",EDGE,{"disambiguationData":[TD([[subQ6,1.0]])],"derivedFrom":subQ5}),1.0]])]});}
            var Q27;
            {var subQ0=sQuery(id+"F2.wireOp",EDGE,"E28");var subQ1=makeQuery(id+"F1.opExtrude","CAP_EDGE",EDGE,{"disambiguationData":[OSD([sQuery(id+"F0.wireOp",EDGE,"E10.trimOffspring")])],"isStart":false});var subQ2=makeQuery(id+"F2.imprint","INTERSECT",VERTEX,{"derivedFrom":[subQ1,subQ0]});Q27=makeQuery(id+"F2.imprint","IMPRINT",FACE,{"disambiguationData":[TD([[makeQuery(id+"F2.imprint","IMPRINT",EDGE,{"disambiguationData":[TD([[subQ2,1.0]])],"derivedFrom":subQ0}),1.0]])]});}
            var Q28;
            {var subQ1=makeQuery(id+"F1.opExtrude","CAP_EDGE",EDGE,{"disambiguationData":[OSD([sQuery(id+"F0.wireOp",EDGE,"E21.6.0")])],"isStart":false});var subQ5=sQuery(id+"F2.wireOp",EDGE,"E28");var subQ6=makeQuery(id+"F2.imprint","INTERSECT",VERTEX,{"derivedFrom":[subQ1,subQ5]});Q28=makeQuery(id+"F2.imprint","IMPRINT",FACE,{"disambiguationData":[TD([[makeQuery(id+"F2.imprint","IMPRINT",EDGE,{"disambiguationData":[TD([[subQ6,-1.0]])],"derivedFrom":subQ5}),1.0]])]});}
            var Q29;
            {var subQ1=makeQuery(id+"F1.opExtrude","CAP_EDGE",EDGE,{"disambiguationData":[OSD([sQuery(id+"F0.wireOp",EDGE,"E21.6.2")])],"isStart":false});var subQ3=sQuery(id+"F2.wireOp",EDGE,"E28");var subQ4=makeQuery(id+"F2.imprint","INTERSECT",VERTEX,{"derivedFrom":[subQ1,subQ3]});Q29=makeQuery(id+"F2.imprint","IMPRINT",FACE,{"disambiguationData":[TD([[makeQuery(id+"F2.imprint","IMPRINT",EDGE,{"disambiguationData":[TD([[subQ4,-1.0]])],"derivedFrom":subQ3}),1.0]])]});}
            var Q30;
            {var subQ5=makeQuery(id+"F1.opExtrude","CAP_EDGE",EDGE,{"disambiguationData":[OSD([sQuery(id+"F0.wireOp",EDGE,"E12.trimOffspring")])],"isStart":false});var subQ7=sQuery(id+"F2.wireOp",EDGE,"E28");var subQ9=makeQuery(id+"F2.imprint","INTERSECT",VERTEX,{"derivedFrom":[subQ5,subQ7]});Q30=makeQuery(id+"F2.imprint","IMPRINT",FACE,{"disambiguationData":[TD([[makeQuery(id+"F2.imprint","IMPRINT",EDGE,{"disambiguationData":[TD([[subQ9,-1.0]])],"derivedFrom":subQ7}),1.0]])]});}
            var Q31;
            {var subQ0=sQuery(id+"F2.wireOp",EDGE,"E28");var subQ1=makeQuery(id+"F1.opExtrude","CAP_EDGE",EDGE,{"disambiguationData":[OSD([sQuery(id+"F0.wireOp",EDGE,"E14.trimOffspring")])],"isStart":false});var subQ2=makeQuery(id+"F2.imprint","INTERSECT",VERTEX,{"derivedFrom":[subQ1,subQ0]});Q31=makeQuery(id+"F2.imprint","IMPRINT",FACE,{"disambiguationData":[TD([[makeQuery(id+"F2.imprint","IMPRINT",EDGE,{"disambiguationData":[TD([[subQ2,-1.0]])],"derivedFrom":subQ0}),1.0]])]});}
            var Q32;
            {var subQ1=makeQuery(id+"F1.opExtrude","CAP_EDGE",EDGE,{"disambiguationData":[OSD([sQuery(id+"F0.wireOp",EDGE,"E21.5.0")])],"isStart":false});var subQ5=sQuery(id+"F2.wireOp",EDGE,"E28");var subQ6=makeQuery(id+"F2.imprint","INTERSECT",VERTEX,{"derivedFrom":[subQ1,subQ5]});Q32=makeQuery(id+"F2.imprint","IMPRINT",FACE,{"disambiguationData":[TD([[makeQuery(id+"F2.imprint","IMPRINT",EDGE,{"disambiguationData":[TD([[subQ6,-1.0]])],"derivedFrom":subQ5}),1.0]])]});}
            var Q33;
            {var subQ1=makeQuery(id+"F1.opExtrude","CAP_EDGE",EDGE,{"disambiguationData":[OSD([sQuery(id+"F0.wireOp",EDGE,"E21.5.2")])],"isStart":false});var subQ3=sQuery(id+"F2.wireOp",EDGE,"E28");var subQ4=makeQuery(id+"F2.imprint","INTERSECT",VERTEX,{"derivedFrom":[subQ1,subQ3]});Q33=makeQuery(id+"F2.imprint","IMPRINT",FACE,{"disambiguationData":[TD([[makeQuery(id+"F2.imprint","IMPRINT",EDGE,{"disambiguationData":[TD([[subQ4,-1.0]])],"derivedFrom":subQ3}),1.0]])]});}
            var Q34;
            {var subQ5=makeQuery(id+"F1.opExtrude","CAP_EDGE",EDGE,{"disambiguationData":[OSD([sQuery(id+"F0.wireOp",EDGE,"E13.trimOffspring")])],"isStart":false});var subQ7=sQuery(id+"F2.wireOp",EDGE,"E28");var subQ9=makeQuery(id+"F2.imprint","INTERSECT",VERTEX,{"derivedFrom":[subQ5,subQ7]});Q34=makeQuery(id+"F2.imprint","IMPRINT",FACE,{"disambiguationData":[TD([[makeQuery(id+"F2.imprint","IMPRINT",EDGE,{"disambiguationData":[TD([[subQ9,-1.0]])],"derivedFrom":subQ7}),1.0]])]});}
            var Q35;
            {var subQ0=sQuery(id+"F2.wireOp",EDGE,"E28");var subQ1=makeQuery(id+"F1.opExtrude","CAP_EDGE",EDGE,{"disambiguationData":[OSD([sQuery(id+"F0.wireOp",EDGE,"E16.trimOffspring")])],"isStart":false});var subQ2=makeQuery(id+"F2.imprint","INTERSECT",VERTEX,{"derivedFrom":[subQ1,subQ0]});Q35=makeQuery(id+"F2.imprint","IMPRINT",FACE,{"disambiguationData":[TD([[makeQuery(id+"F2.imprint","IMPRINT",EDGE,{"disambiguationData":[TD([[subQ2,-1.0]])],"derivedFrom":subQ0}),1.0]])]});}
            var Q36;
            {var subQ1=makeQuery(id+"F1.opExtrude","CAP_EDGE",EDGE,{"disambiguationData":[OSD([sQuery(id+"F0.wireOp",EDGE,"E21.4.0")])],"isStart":false});var subQ7=sQuery(id+"F2.wireOp",EDGE,"E28");var subQ8=makeQuery(id+"F2.imprint","INTERSECT",VERTEX,{"derivedFrom":[subQ1,subQ7]});Q36=makeQuery(id+"F2.imprint","IMPRINT",FACE,{"disambiguationData":[TD([[makeQuery(id+"F2.imprint","IMPRINT",EDGE,{"disambiguationData":[TD([[subQ8,-1.0]])],"derivedFrom":subQ7}),1.0]])]});}
            var Q37;
            {var subQ1=makeQuery(id+"F1.opExtrude","CAP_EDGE",EDGE,{"disambiguationData":[OSD([sQuery(id+"F0.wireOp",EDGE,"E21.4.2")])],"isStart":false});var subQ3=sQuery(id+"F2.wireOp",EDGE,"E28");var subQ4=makeQuery(id+"F2.imprint","INTERSECT",VERTEX,{"derivedFrom":[subQ1,subQ3]});Q37=makeQuery(id+"F2.imprint","IMPRINT",FACE,{"disambiguationData":[TD([[makeQuery(id+"F2.imprint","IMPRINT",EDGE,{"disambiguationData":[TD([[subQ4,-1.0]])],"derivedFrom":subQ3}),1.0]])]});}
            var Q38;
            {var subQ5=sQuery(id+"F2.wireOp",EDGE,"E28");var subQ6=makeQuery(id+"F1.opExtrude","CAP_EDGE",EDGE,{"disambiguationData":[OSD([sQuery(id+"F0.wireOp",EDGE,"E15.trimOffspring")])],"isStart":false});var subQ7=makeQuery(id+"F2.imprint","INTERSECT",VERTEX,{"derivedFrom":[subQ6,subQ5]});Q38=makeQuery(id+"F2.imprint","IMPRINT",FACE,{"disambiguationData":[TD([[makeQuery(id+"F2.imprint","IMPRINT",EDGE,{"disambiguationData":[TD([[subQ7,-1.0]])],"derivedFrom":subQ5}),1.0]])]});}
            var Q39;
            {var subQ0=sQuery(id+"F2.wireOp",EDGE,"E28");var subQ1=makeQuery(id+"F1.opExtrude","CAP_EDGE",EDGE,{"disambiguationData":[OSD([sQuery(id+"F0.wireOp",EDGE,"E18.trimOffspring")])],"isStart":false});var subQ2=makeQuery(id+"F2.imprint","INTERSECT",VERTEX,{"derivedFrom":[subQ1,subQ0]});Q39=makeQuery(id+"F2.imprint","IMPRINT",FACE,{"disambiguationData":[TD([[makeQuery(id+"F2.imprint","IMPRINT",EDGE,{"disambiguationData":[TD([[subQ2,-1.0]])],"derivedFrom":subQ0}),1.0]])]});}
            var Q40;
            {var subQ1=makeQuery(id+"F1.opExtrude","CAP_EDGE",EDGE,{"disambiguationData":[OSD([sQuery(id+"F0.wireOp",EDGE,"E21.3.0")])],"isStart":false});var subQ5=sQuery(id+"F2.wireOp",EDGE,"E28");var subQ6=makeQuery(id+"F2.imprint","INTERSECT",VERTEX,{"derivedFrom":[subQ1,subQ5]});Q40=makeQuery(id+"F2.imprint","IMPRINT",FACE,{"disambiguationData":[TD([[makeQuery(id+"F2.imprint","IMPRINT",EDGE,{"disambiguationData":[TD([[subQ6,-1.0]])],"derivedFrom":subQ5}),1.0]])]});}
            var Q41;
            {var subQ1=makeQuery(id+"F1.opExtrude","CAP_EDGE",EDGE,{"disambiguationData":[OSD([sQuery(id+"F0.wireOp",EDGE,"E21.3.2")])],"isStart":false});var subQ3=sQuery(id+"F2.wireOp",EDGE,"E28");var subQ4=makeQuery(id+"F2.imprint","INTERSECT",VERTEX,{"derivedFrom":[subQ1,subQ3]});Q41=makeQuery(id+"F2.imprint","IMPRINT",FACE,{"disambiguationData":[TD([[makeQuery(id+"F2.imprint","IMPRINT",EDGE,{"disambiguationData":[TD([[subQ4,-1.0]])],"derivedFrom":subQ3}),1.0]])]});}
            var Q42;
            {var subQ5=makeQuery(id+"F1.opExtrude","CAP_EDGE",EDGE,{"disambiguationData":[OSD([sQuery(id+"F0.wireOp",EDGE,"E17.trimOffspring")])],"isStart":false});var subQ7=sQuery(id+"F2.wireOp",EDGE,"E28");var subQ9=makeQuery(id+"F2.imprint","INTERSECT",VERTEX,{"derivedFrom":[subQ5,subQ7]});Q42=makeQuery(id+"F2.imprint","IMPRINT",FACE,{"disambiguationData":[TD([[makeQuery(id+"F2.imprint","IMPRINT",EDGE,{"disambiguationData":[TD([[subQ9,-1.0]])],"derivedFrom":subQ7}),1.0]])]});}
            var Q43;
            {var subQ0=sQuery(id+"F2.wireOp",EDGE,"E28");var subQ1=makeQuery(id+"F1.opExtrude","CAP_EDGE",EDGE,{"disambiguationData":[OSD([sQuery(id+"F0.wireOp",EDGE,"E6.trimOffspring")])],"isStart":false});var subQ2=makeQuery(id+"F2.imprint","INTERSECT",VERTEX,{"derivedFrom":[subQ1,subQ0]});Q43=makeQuery(id+"F2.imprint","IMPRINT",FACE,{"disambiguationData":[TD([[makeQuery(id+"F2.imprint","IMPRINT",EDGE,{"disambiguationData":[TD([[subQ2,-1.0]])],"derivedFrom":subQ0}),1.0]])]});}
            var Q44;
            {var subQ1=makeQuery(id+"F1.opExtrude","CAP_EDGE",EDGE,{"disambiguationData":[OSD([sQuery(id+"F0.wireOp",EDGE,"E21.2.0")])],"isStart":false});var subQ5=sQuery(id+"F2.wireOp",EDGE,"E28");var subQ6=makeQuery(id+"F2.imprint","INTERSECT",VERTEX,{"derivedFrom":[subQ1,subQ5]});Q44=makeQuery(id+"F2.imprint","IMPRINT",FACE,{"disambiguationData":[TD([[makeQuery(id+"F2.imprint","IMPRINT",EDGE,{"disambiguationData":[TD([[subQ6,-1.0]])],"derivedFrom":subQ5}),1.0]])]});}
            var Q45;
            {var subQ1=makeQuery(id+"F1.opExtrude","CAP_EDGE",EDGE,{"disambiguationData":[OSD([sQuery(id+"F0.wireOp",EDGE,"E21.2.2")])],"isStart":false});var subQ3=sQuery(id+"F2.wireOp",EDGE,"E28");var subQ4=makeQuery(id+"F2.imprint","INTERSECT",VERTEX,{"derivedFrom":[subQ1,subQ3]});Q45=makeQuery(id+"F2.imprint","IMPRINT",FACE,{"disambiguationData":[TD([[makeQuery(id+"F2.imprint","IMPRINT",EDGE,{"disambiguationData":[TD([[subQ4,-1.0]])],"derivedFrom":subQ3}),1.0]])]});}
            var Q46;
            {var subQ5=makeQuery(id+"F1.opExtrude","CAP_EDGE",EDGE,{"disambiguationData":[OSD([sQuery(id+"F0.wireOp",EDGE,"E19.trimOffspring")])],"isStart":false});var subQ7=sQuery(id+"F2.wireOp",EDGE,"E28");var subQ9=makeQuery(id+"F2.imprint","INTERSECT",VERTEX,{"derivedFrom":[subQ5,subQ7]});Q46=makeQuery(id+"F2.imprint","IMPRINT",FACE,{"disambiguationData":[TD([[makeQuery(id+"F2.imprint","IMPRINT",EDGE,{"disambiguationData":[TD([[subQ9,-1.0]])],"derivedFrom":subQ7}),1.0]])]});}
            var Q47;
            {var subQ0=sQuery(id+"F2.wireOp",EDGE,"E28");var subQ1=makeQuery(id+"F1.opExtrude","CAP_EDGE",EDGE,{"disambiguationData":[OSD([sQuery(id+"F0.wireOp",EDGE,"E7.trimOffspring")])],"isStart":false});var subQ2=makeQuery(id+"F2.imprint","INTERSECT",VERTEX,{"derivedFrom":[subQ1,subQ0]});Q47=makeQuery(id+"F2.imprint","IMPRINT",FACE,{"disambiguationData":[TD([[makeQuery(id+"F2.imprint","IMPRINT",EDGE,{"disambiguationData":[TD([[subQ2,-1.0]])],"derivedFrom":subQ0}),1.0]])]});}
            var Q48;
            {var subQ1=makeQuery(id+"F1.opExtrude","CAP_EDGE",EDGE,{"disambiguationData":[OSD([sQuery(id+"F0.wireOp",EDGE,"E21.1.0")])],"isStart":false});var subQ5=sQuery(id+"F2.wireOp",EDGE,"E28");var subQ6=makeQuery(id+"F2.imprint","INTERSECT",VERTEX,{"derivedFrom":[subQ1,subQ5]});Q48=makeQuery(id+"F2.imprint","IMPRINT",FACE,{"disambiguationData":[TD([[makeQuery(id+"F2.imprint","IMPRINT",EDGE,{"disambiguationData":[TD([[subQ6,-1.0]])],"derivedFrom":subQ5}),1.0]])]});}
            var Q49;
            {var subQ1=makeQuery(id+"F1.opExtrude","CAP_EDGE",EDGE,{"disambiguationData":[OSD([sQuery(id+"F0.wireOp",EDGE,"E21.1.2")])],"isStart":false});var subQ3=sQuery(id+"F2.wireOp",EDGE,"E28");var subQ4=makeQuery(id+"F2.imprint","INTERSECT",VERTEX,{"derivedFrom":[subQ1,subQ3]});Q49=makeQuery(id+"F2.imprint","IMPRINT",FACE,{"disambiguationData":[TD([[makeQuery(id+"F2.imprint","IMPRINT",EDGE,{"disambiguationData":[TD([[subQ4,-1.0]])],"derivedFrom":subQ3}),1.0]])]});}
            var Q50;
            {var subQ5=makeQuery(id+"F1.opExtrude","CAP_EDGE",EDGE,{"disambiguationData":[OSD([sQuery(id+"F0.wireOp",EDGE,"E5.trimOffspring")])],"isStart":false});var subQ7=sQuery(id+"F2.wireOp",EDGE,"E28");var subQ8=makeQuery(id+"F2.imprint","INTERSECT",VERTEX,{"derivedFrom":[subQ5,subQ7]});Q50=makeQuery(id+"F2.imprint","IMPRINT",FACE,{"disambiguationData":[TD([[makeQuery(id+"F2.imprint","IMPRINT",EDGE,{"disambiguationData":[TD([[subQ8,-1.0]])],"derivedFrom":subQ7}),1.0]])]});}
            var Q51;
            {var subQ0=sQuery(id+"F2.wireOp",EDGE,"E28");var subQ1=makeQuery(id+"F1.opExtrude","CAP_EDGE",EDGE,{"disambiguationData":[OSD([sQuery(id+"F0.wireOp",EDGE,"E9.trimOffspring")])],"isStart":false});var subQ2=makeQuery(id+"F2.imprint","INTERSECT",VERTEX,{"derivedFrom":[subQ1,subQ0]});Q51=makeQuery(id+"F2.imprint","IMPRINT",FACE,{"disambiguationData":[TD([[makeQuery(id+"F2.imprint","IMPRINT",EDGE,{"disambiguationData":[TD([[subQ2,-1.0]])],"derivedFrom":subQ0}),1.0]])]});}
            var Q52;
            {var subQ0=makeQuery(id+"F1.opExtrude","CAP_EDGE",EDGE,{"disambiguationData":[OSD([sQuery(id+"F0.wireOp",EDGE,"E2.0.left")])],"isStart":false});var subQ3=sQuery(id+"F2.wireOp",EDGE,"E28");var subQ4=makeQuery(id+"F2.imprint","INTERSECT",VERTEX,{"derivedFrom":[subQ0,subQ3]});Q52=makeQuery(id+"F2.imprint","IMPRINT",FACE,{"disambiguationData":[TD([[makeQuery(id+"F2.imprint","IMPRINT",EDGE,{"disambiguationData":[TD([[subQ4,-1.0]])],"derivedFrom":subQ3}),1.0]])]});}
            var Q53;
            {var subQ5=sQuery(id+"F2.wireOp",EDGE,"E28");var subQ6=makeQuery(id+"F1.opExtrude","CAP_EDGE",EDGE,{"disambiguationData":[OSD([sQuery(id+"F0.wireOp",EDGE,"E2.0.right")])],"isStart":false});var subQ7=makeQuery(id+"F2.imprint","INTERSECT",VERTEX,{"derivedFrom":[subQ6,subQ5]});Q53=makeQuery(id+"F2.imprint","IMPRINT",FACE,{"disambiguationData":[TD([[makeQuery(id+"F2.imprint","IMPRINT",EDGE,{"disambiguationData":[TD([[subQ7,-1.0]])],"derivedFrom":subQ5}),1.0]])]});}
            var Q54;
            {var subQ5=sQuery(id+"F2.wireOp",EDGE,"E28");var subQ6=makeQuery(id+"F1.opExtrude","CAP_EDGE",EDGE,{"disambiguationData":[OSD([sQuery(id+"F0.wireOp",EDGE,"E8.trimOffspring")])],"isStart":false});var subQ7=makeQuery(id+"F2.imprint","INTERSECT",VERTEX,{"derivedFrom":[subQ6,subQ5]});Q54=makeQuery(id+"F2.imprint","IMPRINT",FACE,{"disambiguationData":[TD([[makeQuery(id+"F2.imprint","IMPRINT",EDGE,{"disambiguationData":[TD([[subQ7,-1.0]])],"derivedFrom":subQ5}),1.0]])]});}
            var Q55;
            {var subQ1=makeQuery(id+"F1.opExtrude","CAP_EDGE",EDGE,{"disambiguationData":[OSD([sQuery(id+"F0.wireOp",EDGE,"E21.7.0")])],"isStart":false});var subQ7=sQuery(id+"F2.wireOp",EDGE,"E28");var subQ8=makeQuery(id+"F2.imprint","INTERSECT",VERTEX,{"derivedFrom":[subQ1,subQ7]});Q55=makeQuery(id+"F2.imprint","IMPRINT",FACE,{"disambiguationData":[TD([[makeQuery(id+"F2.imprint","IMPRINT",EDGE,{"disambiguationData":[TD([[subQ8,-1.0]])],"derivedFrom":subQ7}),1.0]])]});}
            var Q56;
            {var subQ0=sQuery(id+"F2.wireOp",EDGE,"E28");var subQ1=makeQuery(id+"F1.opExtrude","CAP_EDGE",EDGE,{"disambiguationData":[OSD([sQuery(id+"F0.wireOp",EDGE,"E11.trimOffspring")])],"isStart":false});var subQ2=makeQuery(id+"F2.imprint","INTERSECT",VERTEX,{"derivedFrom":[subQ1,subQ0]});Q56=makeQuery(id+"F2.imprint","IMPRINT",FACE,{"disambiguationData":[TD([[makeQuery(id+"F2.imprint","IMPRINT",EDGE,{"disambiguationData":[TD([[subQ2,-1.0]])],"derivedFrom":subQ0}),1.0]])]});}
            var Q57;
            {var subQ0=sQuery(id+"F2.wireOp",EDGE,"E23");var subQ1=makeQuery(id+"F1.opExtrude","CAP_EDGE",EDGE,{"disambiguationData":[OSD([sQuery(id+"F0.wireOp",EDGE,"E2.0.right")])],"isStart":false});var subQ2=makeQuery(id+"F2.imprint","INTERSECT",VERTEX,{"derivedFrom":[subQ1,subQ0]});Q57=makeQuery(id+"F2.imprint","IMPRINT",FACE,{"disambiguationData":[TD([[makeQuery(id+"F2.imprint","IMPRINT",EDGE,{"disambiguationData":[TD([[subQ2,-1.0]])],"derivedFrom":subQ0}),1.0]])]});}
            var Q58;
            {var subQ5=makeQuery(id+"F1.opExtrude","CAP_EDGE",EDGE,{"disambiguationData":[OSD([sQuery(id+"F0.wireOp",EDGE,"E22.15.3")])],"isStart":false});Q58=makeQuery(id+"F2.imprint","IMPRINT",FACE,{"disambiguationData":[TD([[makeQuery(id+"F2.imprint","IMPRINT",EDGE,{"derivedFrom":subQ5}),-1.0]])]});}
            var Q59;
            {var subQ0=makeQuery(id+"F1.opExtrude","CAP_EDGE",EDGE,{"disambiguationData":[OSD([sQuery(id+"F0.wireOp",EDGE,"E22.15.3")])],"isStart":false});Q59=makeQuery(id+"F2.imprint","IMPRINT",FACE,{"disambiguationData":[TD([[makeQuery(id+"F2.imprint","IMPRINT",EDGE,{"derivedFrom":subQ0}),1.0]])]});}
            var Q60;
            {var subQ0=sQuery(id+"F2.wireOp",EDGE,"E23");var subQ1=makeQuery(id+"F1.opExtrude","CAP_EDGE",EDGE,{"disambiguationData":[OSD([sQuery(id+"F0.wireOp",EDGE,"E11.trimOffspring")])],"isStart":false});var subQ2=makeQuery(id+"F2.imprint","INTERSECT",VERTEX,{"derivedFrom":[subQ1,subQ0]});Q60=makeQuery(id+"F2.imprint","IMPRINT",FACE,{"disambiguationData":[TD([[makeQuery(id+"F2.imprint","IMPRINT",EDGE,{"disambiguationData":[TD([[subQ2,-1.0]])],"derivedFrom":subQ0}),1.0]])]});}
            var Q61;
            {var subQ12=makeQuery(id+"F1.opExtrude","CAP_EDGE",EDGE,{"disambiguationData":[OSD([sQuery(id+"F0.wireOp",EDGE,"E22.14.3")])],"isStart":false});Q61=makeQuery(id+"F2.imprint","IMPRINT",FACE,{"disambiguationData":[TD([[makeQuery(id+"F2.imprint","IMPRINT",EDGE,{"derivedFrom":subQ12}),1.0]])]});}
            var Q62;
            {var subQ0=sQuery(id+"F2.wireOp",EDGE,"E23");var subQ1=makeQuery(id+"F1.opExtrude","CAP_EDGE",EDGE,{"disambiguationData":[OSD([sQuery(id+"F0.wireOp",EDGE,"E11.trimOffspring")])],"isStart":false});var subQ2=makeQuery(id+"F2.imprint","INTERSECT",VERTEX,{"derivedFrom":[subQ1,subQ0]});Q62=makeQuery(id+"F2.imprint","IMPRINT",FACE,{"disambiguationData":[TD([[makeQuery(id+"F2.imprint","IMPRINT",EDGE,{"disambiguationData":[TD([[subQ2,-1.0]])],"derivedFrom":subQ0}),1.0]])]});}
            var Q63;
            {var subQ0=sQuery(id+"F2.wireOp",EDGE,"E23");var subQ1=makeQuery(id+"F1.opExtrude","CAP_EDGE",EDGE,{"disambiguationData":[OSD([sQuery(id+"F0.wireOp",EDGE,"E21.7.2")])],"isStart":false});var subQ2=makeQuery(id+"F2.imprint","INTERSECT",VERTEX,{"derivedFrom":[subQ1,subQ0]});Q63=makeQuery(id+"F2.imprint","IMPRINT",FACE,{"disambiguationData":[TD([[makeQuery(id+"F2.imprint","IMPRINT",EDGE,{"disambiguationData":[TD([[subQ2,-1.0]])],"derivedFrom":subQ0}),1.0]])]});}
            var Q64;
            {var subQ0=makeQuery(id+"F1.opExtrude","CAP_EDGE",EDGE,{"disambiguationData":[OSD([sQuery(id+"F0.wireOp",EDGE,"E22.13.3")])],"isStart":false});Q64=makeQuery(id+"F2.imprint","IMPRINT",FACE,{"disambiguationData":[TD([[makeQuery(id+"F2.imprint","IMPRINT",EDGE,{"derivedFrom":subQ0}),1.0]])]});}
            var Q65;
            {var subQ0=sQuery(id+"F2.wireOp",EDGE,"E23");var subQ1=makeQuery(id+"F1.opExtrude","CAP_EDGE",EDGE,{"disambiguationData":[OSD([sQuery(id+"F0.wireOp",EDGE,"E10.trimOffspring")])],"isStart":false});var subQ2=makeQuery(id+"F2.imprint","INTERSECT",VERTEX,{"derivedFrom":[subQ1,subQ0]});Q65=makeQuery(id+"F2.imprint","IMPRINT",FACE,{"disambiguationData":[TD([[makeQuery(id+"F2.imprint","IMPRINT",EDGE,{"disambiguationData":[TD([[subQ2,1.0]])],"derivedFrom":subQ0}),1.0]])]});}
            var Q66;
            {var subQ5=makeQuery(id+"F1.opExtrude","CAP_EDGE",EDGE,{"disambiguationData":[OSD([sQuery(id+"F0.wireOp",EDGE,"E22.12.3")])],"isStart":false});Q66=makeQuery(id+"F2.imprint","IMPRINT",FACE,{"disambiguationData":[TD([[makeQuery(id+"F2.imprint","IMPRINT",EDGE,{"derivedFrom":subQ5}),1.0]])]});}
            var Q67;
            {var subQ0=sQuery(id+"F2.wireOp",EDGE,"E23");var subQ1=makeQuery(id+"F1.opExtrude","CAP_EDGE",EDGE,{"disambiguationData":[OSD([sQuery(id+"F0.wireOp",EDGE,"E21.6.2")])],"isStart":false});var subQ2=makeQuery(id+"F2.imprint","INTERSECT",VERTEX,{"derivedFrom":[subQ1,subQ0]});Q67=makeQuery(id+"F2.imprint","IMPRINT",FACE,{"disambiguationData":[TD([[makeQuery(id+"F2.imprint","IMPRINT",EDGE,{"disambiguationData":[TD([[subQ2,-1.0]])],"derivedFrom":subQ0}),1.0]])]});}
            var Q68;
            {var subQ0=makeQuery(id+"F1.opExtrude","CAP_EDGE",EDGE,{"disambiguationData":[OSD([sQuery(id+"F0.wireOp",EDGE,"E22.11.3")])],"isStart":false});Q68=makeQuery(id+"F2.imprint","IMPRINT",FACE,{"disambiguationData":[TD([[makeQuery(id+"F2.imprint","IMPRINT",EDGE,{"derivedFrom":subQ0}),1.0]])]});}
            var Q69;
            {var subQ0=sQuery(id+"F2.wireOp",EDGE,"E23");var subQ1=makeQuery(id+"F1.opExtrude","CAP_EDGE",EDGE,{"disambiguationData":[OSD([sQuery(id+"F0.wireOp",EDGE,"E14.trimOffspring")])],"isStart":false});var subQ2=makeQuery(id+"F2.imprint","INTERSECT",VERTEX,{"derivedFrom":[subQ1,subQ0]});Q69=makeQuery(id+"F2.imprint","IMPRINT",FACE,{"disambiguationData":[TD([[makeQuery(id+"F2.imprint","IMPRINT",EDGE,{"disambiguationData":[TD([[subQ2,-1.0]])],"derivedFrom":subQ0}),1.0]])]});}
            var Q70;
            {var subQ0=makeQuery(id+"F1.opExtrude","CAP_EDGE",EDGE,{"disambiguationData":[OSD([sQuery(id+"F0.wireOp",EDGE,"E22.10.3")])],"isStart":false});Q70=makeQuery(id+"F2.imprint","IMPRINT",FACE,{"disambiguationData":[TD([[makeQuery(id+"F2.imprint","IMPRINT",EDGE,{"derivedFrom":subQ0}),1.0]])]});}
            var Q71;
            {var subQ0=sQuery(id+"F2.wireOp",EDGE,"E23");var subQ1=makeQuery(id+"F1.opExtrude","CAP_EDGE",EDGE,{"disambiguationData":[OSD([sQuery(id+"F0.wireOp",EDGE,"E21.5.2")])],"isStart":false});var subQ2=makeQuery(id+"F2.imprint","INTERSECT",VERTEX,{"derivedFrom":[subQ1,subQ0]});Q71=makeQuery(id+"F2.imprint","IMPRINT",FACE,{"disambiguationData":[TD([[makeQuery(id+"F2.imprint","IMPRINT",EDGE,{"disambiguationData":[TD([[subQ2,-1.0]])],"derivedFrom":subQ0}),1.0]])]});}
            var Q72;
            {var subQ0=makeQuery(id+"F1.opExtrude","CAP_EDGE",EDGE,{"disambiguationData":[OSD([sQuery(id+"F0.wireOp",EDGE,"E22.9.3")])],"isStart":false});Q72=makeQuery(id+"F2.imprint","IMPRINT",FACE,{"disambiguationData":[TD([[makeQuery(id+"F2.imprint","IMPRINT",EDGE,{"derivedFrom":subQ0}),1.0]])]});}
            var Q73;
            {var subQ0=sQuery(id+"F2.wireOp",EDGE,"E23");var subQ1=makeQuery(id+"F1.opExtrude","CAP_EDGE",EDGE,{"disambiguationData":[OSD([sQuery(id+"F0.wireOp",EDGE,"E16.trimOffspring")])],"isStart":false});var subQ2=makeQuery(id+"F2.imprint","INTERSECT",VERTEX,{"derivedFrom":[subQ1,subQ0]});Q73=makeQuery(id+"F2.imprint","IMPRINT",FACE,{"disambiguationData":[TD([[makeQuery(id+"F2.imprint","IMPRINT",EDGE,{"disambiguationData":[TD([[subQ2,-1.0]])],"derivedFrom":subQ0}),1.0]])]});}
            var Q74;
            {var subQ0=makeQuery(id+"F1.opExtrude","CAP_EDGE",EDGE,{"disambiguationData":[OSD([sQuery(id+"F0.wireOp",EDGE,"E22.8.3")])],"isStart":false});Q74=makeQuery(id+"F2.imprint","IMPRINT",FACE,{"disambiguationData":[TD([[makeQuery(id+"F2.imprint","IMPRINT",EDGE,{"derivedFrom":subQ0}),1.0]])]});}
            var Q75;
            {var subQ0=sQuery(id+"F2.wireOp",EDGE,"E23");var subQ1=makeQuery(id+"F1.opExtrude","CAP_EDGE",EDGE,{"disambiguationData":[OSD([sQuery(id+"F0.wireOp",EDGE,"E21.4.2")])],"isStart":false});var subQ2=makeQuery(id+"F2.imprint","INTERSECT",VERTEX,{"derivedFrom":[subQ1,subQ0]});Q75=makeQuery(id+"F2.imprint","IMPRINT",FACE,{"disambiguationData":[TD([[makeQuery(id+"F2.imprint","IMPRINT",EDGE,{"disambiguationData":[TD([[subQ2,-1.0]])],"derivedFrom":subQ0}),1.0]])]});}
            var Q76;
            {var subQ5=makeQuery(id+"F1.opExtrude","CAP_EDGE",EDGE,{"disambiguationData":[OSD([sQuery(id+"F0.wireOp",EDGE,"E22.7.3")])],"isStart":false});Q76=makeQuery(id+"F2.imprint","IMPRINT",FACE,{"disambiguationData":[TD([[makeQuery(id+"F2.imprint","IMPRINT",EDGE,{"derivedFrom":subQ5}),1.0]])]});}
            var Q77;
            {var subQ0=sQuery(id+"F2.wireOp",EDGE,"E23");var subQ1=makeQuery(id+"F1.opExtrude","CAP_EDGE",EDGE,{"disambiguationData":[OSD([sQuery(id+"F0.wireOp",EDGE,"E18.trimOffspring")])],"isStart":false});var subQ2=makeQuery(id+"F2.imprint","INTERSECT",VERTEX,{"derivedFrom":[subQ1,subQ0]});Q77=makeQuery(id+"F2.imprint","IMPRINT",FACE,{"disambiguationData":[TD([[makeQuery(id+"F2.imprint","IMPRINT",EDGE,{"disambiguationData":[TD([[subQ2,-1.0]])],"derivedFrom":subQ0}),1.0]])]});}
            var Q78;
            {var subQ0=makeQuery(id+"F1.opExtrude","CAP_EDGE",EDGE,{"disambiguationData":[OSD([sQuery(id+"F0.wireOp",EDGE,"E22.6.3")])],"isStart":false});Q78=makeQuery(id+"F2.imprint","IMPRINT",FACE,{"disambiguationData":[TD([[makeQuery(id+"F2.imprint","IMPRINT",EDGE,{"derivedFrom":subQ0}),1.0]])]});}
            var Q79;
            {var subQ0=sQuery(id+"F2.wireOp",EDGE,"E23");var subQ1=makeQuery(id+"F1.opExtrude","CAP_EDGE",EDGE,{"disambiguationData":[OSD([sQuery(id+"F0.wireOp",EDGE,"E21.3.2")])],"isStart":false});var subQ2=makeQuery(id+"F2.imprint","INTERSECT",VERTEX,{"derivedFrom":[subQ1,subQ0]});Q79=makeQuery(id+"F2.imprint","IMPRINT",FACE,{"disambiguationData":[TD([[makeQuery(id+"F2.imprint","IMPRINT",EDGE,{"disambiguationData":[TD([[subQ2,-1.0]])],"derivedFrom":subQ0}),1.0]])]});}
            var Q80;
            {var subQ0=makeQuery(id+"F1.opExtrude","CAP_EDGE",EDGE,{"disambiguationData":[OSD([sQuery(id+"F0.wireOp",EDGE,"E22.5.3")])],"isStart":false});Q80=makeQuery(id+"F2.imprint","IMPRINT",FACE,{"disambiguationData":[TD([[makeQuery(id+"F2.imprint","IMPRINT",EDGE,{"derivedFrom":subQ0}),1.0]])]});}
            var Q81;
            {var subQ0=sQuery(id+"F2.wireOp",EDGE,"E23");var subQ1=makeQuery(id+"F1.opExtrude","CAP_EDGE",EDGE,{"disambiguationData":[OSD([sQuery(id+"F0.wireOp",EDGE,"E6.trimOffspring")])],"isStart":false});var subQ2=makeQuery(id+"F2.imprint","INTERSECT",VERTEX,{"derivedFrom":[subQ1,subQ0]});Q81=makeQuery(id+"F2.imprint","IMPRINT",FACE,{"disambiguationData":[TD([[makeQuery(id+"F2.imprint","IMPRINT",EDGE,{"disambiguationData":[TD([[subQ2,-1.0]])],"derivedFrom":subQ0}),1.0]])]});}
            var Q82;
            {var subQ0=makeQuery(id+"F1.opExtrude","CAP_EDGE",EDGE,{"disambiguationData":[OSD([sQuery(id+"F0.wireOp",EDGE,"E22.4.3")])],"isStart":false});Q82=makeQuery(id+"F2.imprint","IMPRINT",FACE,{"disambiguationData":[TD([[makeQuery(id+"F2.imprint","IMPRINT",EDGE,{"derivedFrom":subQ0}),1.0]])]});}
            var Q83;
            {var subQ0=sQuery(id+"F2.wireOp",EDGE,"E23");var subQ1=makeQuery(id+"F1.opExtrude","CAP_EDGE",EDGE,{"disambiguationData":[OSD([sQuery(id+"F0.wireOp",EDGE,"E21.2.2")])],"isStart":false});var subQ2=makeQuery(id+"F2.imprint","INTERSECT",VERTEX,{"derivedFrom":[subQ1,subQ0]});Q83=makeQuery(id+"F2.imprint","IMPRINT",FACE,{"disambiguationData":[TD([[makeQuery(id+"F2.imprint","IMPRINT",EDGE,{"disambiguationData":[TD([[subQ2,-1.0]])],"derivedFrom":subQ0}),1.0]])]});}
            var Q84;
            {var subQ0=makeQuery(id+"F1.opExtrude","CAP_EDGE",EDGE,{"disambiguationData":[OSD([sQuery(id+"F0.wireOp",EDGE,"E22.3.3")])],"isStart":false});Q84=makeQuery(id+"F2.imprint","IMPRINT",FACE,{"disambiguationData":[TD([[makeQuery(id+"F2.imprint","IMPRINT",EDGE,{"derivedFrom":subQ0}),1.0]])]});}
            var Q85;
            {var subQ0=sQuery(id+"F2.wireOp",EDGE,"E23");var subQ1=makeQuery(id+"F1.opExtrude","CAP_EDGE",EDGE,{"disambiguationData":[OSD([sQuery(id+"F0.wireOp",EDGE,"E7.trimOffspring")])],"isStart":false});var subQ2=makeQuery(id+"F2.imprint","INTERSECT",VERTEX,{"derivedFrom":[subQ1,subQ0]});Q85=makeQuery(id+"F2.imprint","IMPRINT",FACE,{"disambiguationData":[TD([[makeQuery(id+"F2.imprint","IMPRINT",EDGE,{"disambiguationData":[TD([[subQ2,-1.0]])],"derivedFrom":subQ0}),1.0]])]});}
            var Q86;
            {var subQ5=makeQuery(id+"F1.opExtrude","CAP_EDGE",EDGE,{"disambiguationData":[OSD([sQuery(id+"F0.wireOp",EDGE,"E22.2.3")])],"isStart":false});Q86=makeQuery(id+"F2.imprint","IMPRINT",FACE,{"disambiguationData":[TD([[makeQuery(id+"F2.imprint","IMPRINT",EDGE,{"derivedFrom":subQ5}),1.0]])]});}
            var Q87;
            {var subQ0=sQuery(id+"F2.wireOp",EDGE,"E23");var subQ1=makeQuery(id+"F1.opExtrude","CAP_EDGE",EDGE,{"disambiguationData":[OSD([sQuery(id+"F0.wireOp",EDGE,"E21.1.2")])],"isStart":false});var subQ2=makeQuery(id+"F2.imprint","INTERSECT",VERTEX,{"derivedFrom":[subQ1,subQ0]});Q87=makeQuery(id+"F2.imprint","IMPRINT",FACE,{"disambiguationData":[TD([[makeQuery(id+"F2.imprint","IMPRINT",EDGE,{"disambiguationData":[TD([[subQ2,-1.0]])],"derivedFrom":subQ0}),1.0]])]});}
            var Q88;
            {var subQ0=makeQuery(id+"F1.opExtrude","CAP_EDGE",EDGE,{"disambiguationData":[OSD([sQuery(id+"F0.wireOp",EDGE,"E22.1.3")])],"isStart":false});Q88=makeQuery(id+"F2.imprint","IMPRINT",FACE,{"disambiguationData":[TD([[makeQuery(id+"F2.imprint","IMPRINT",EDGE,{"derivedFrom":subQ0}),1.0]])]});}
            var Q89;
            {var subQ0=sQuery(id+"F2.wireOp",EDGE,"E23");var subQ1=makeQuery(id+"F1.opExtrude","CAP_EDGE",EDGE,{"disambiguationData":[OSD([sQuery(id+"F0.wireOp",EDGE,"E9.trimOffspring")])],"isStart":false});var subQ2=makeQuery(id+"F2.imprint","INTERSECT",VERTEX,{"derivedFrom":[subQ1,subQ0]});Q89=makeQuery(id+"F2.imprint","IMPRINT",FACE,{"disambiguationData":[TD([[makeQuery(id+"F2.imprint","IMPRINT",EDGE,{"disambiguationData":[TD([[subQ2,-1.0]])],"derivedFrom":subQ0}),1.0]])]});}
            var Q90;
            {var subQ0=makeQuery(id+"F1.opExtrude","CAP_EDGE",EDGE,{"disambiguationData":[OSD([sQuery(id+"F0.wireOp",EDGE,"E3.0.endCap")])],"isStart":false});Q90=makeQuery(id+"F2.imprint","IMPRINT",FACE,{"disambiguationData":[TD([[makeQuery(id+"F2.imprint","IMPRINT",EDGE,{"derivedFrom":subQ0}),1.0]])]});}
            var Q91;
            {var subQ5=makeQuery(id+"F1.opExtrude","CAP_EDGE",EDGE,{"disambiguationData":[OSD([sQuery(id+"F0.wireOp",EDGE,"E22.9.3")])],"isStart":false});Q91=makeQuery(id+"F2.imprint","IMPRINT",FACE,{"disambiguationData":[TD([[makeQuery(id+"F2.imprint","IMPRINT",EDGE,{"derivedFrom":subQ5}),-1.0]])]});}
            var Q92;
            {var subQ5=makeQuery(id+"F1.opExtrude","CAP_EDGE",EDGE,{"disambiguationData":[OSD([sQuery(id+"F0.wireOp",EDGE,"E22.10.3")])],"isStart":false});Q92=makeQuery(id+"F2.imprint","IMPRINT",FACE,{"disambiguationData":[TD([[makeQuery(id+"F2.imprint","IMPRINT",EDGE,{"derivedFrom":subQ5}),-1.0]])]});}
            var Q93;
            {var subQ5=makeQuery(id+"F1.opExtrude","CAP_EDGE",EDGE,{"disambiguationData":[OSD([sQuery(id+"F0.wireOp",EDGE,"E22.11.3")])],"isStart":false});Q93=makeQuery(id+"F2.imprint","IMPRINT",FACE,{"disambiguationData":[TD([[makeQuery(id+"F2.imprint","IMPRINT",EDGE,{"derivedFrom":subQ5}),-1.0]])]});}
            var Q94;
            {var subQ5=makeQuery(id+"F1.opExtrude","CAP_EDGE",EDGE,{"disambiguationData":[OSD([sQuery(id+"F0.wireOp",EDGE,"E22.12.3")])],"isStart":false});Q94=makeQuery(id+"F2.imprint","IMPRINT",FACE,{"disambiguationData":[TD([[makeQuery(id+"F2.imprint","IMPRINT",EDGE,{"derivedFrom":subQ5}),-1.0]])]});}
            var Q95;
            {var subQ5=makeQuery(id+"F1.opExtrude","CAP_EDGE",EDGE,{"disambiguationData":[OSD([sQuery(id+"F0.wireOp",EDGE,"E22.13.3")])],"isStart":false});Q95=makeQuery(id+"F2.imprint","IMPRINT",FACE,{"disambiguationData":[TD([[makeQuery(id+"F2.imprint","IMPRINT",EDGE,{"derivedFrom":subQ5}),-1.0]])]});}
            var Q96;
            {var subQ5=makeQuery(id+"F1.opExtrude","CAP_EDGE",EDGE,{"disambiguationData":[OSD([sQuery(id+"F0.wireOp",EDGE,"E22.14.3")])],"isStart":false});Q96=makeQuery(id+"F2.imprint","IMPRINT",FACE,{"disambiguationData":[TD([[makeQuery(id+"F2.imprint","IMPRINT",EDGE,{"derivedFrom":subQ5}),-1.0]])]});}
            var Q97;
            {var subQ5=makeQuery(id+"F1.opExtrude","CAP_EDGE",EDGE,{"disambiguationData":[OSD([sQuery(id+"F0.wireOp",EDGE,"E3.0.endCap")])],"isStart":false});Q97=makeQuery(id+"F2.imprint","IMPRINT",FACE,{"disambiguationData":[TD([[makeQuery(id+"F2.imprint","IMPRINT",EDGE,{"derivedFrom":subQ5}),-1.0]])]});}
            var Q98;
            {var subQ5=makeQuery(id+"F1.opExtrude","CAP_EDGE",EDGE,{"disambiguationData":[OSD([sQuery(id+"F0.wireOp",EDGE,"E22.1.3")])],"isStart":false});Q98=makeQuery(id+"F2.imprint","IMPRINT",FACE,{"disambiguationData":[TD([[makeQuery(id+"F2.imprint","IMPRINT",EDGE,{"derivedFrom":subQ5}),-1.0]])]});}
            var Q99;
            {var subQ5=makeQuery(id+"F1.opExtrude","CAP_EDGE",EDGE,{"disambiguationData":[OSD([sQuery(id+"F0.wireOp",EDGE,"E22.2.3")])],"isStart":false});Q99=makeQuery(id+"F2.imprint","IMPRINT",FACE,{"disambiguationData":[TD([[makeQuery(id+"F2.imprint","IMPRINT",EDGE,{"derivedFrom":subQ5}),-1.0]])]});}
            var Q100;
            {var subQ5=makeQuery(id+"F1.opExtrude","CAP_EDGE",EDGE,{"disambiguationData":[OSD([sQuery(id+"F0.wireOp",EDGE,"E22.3.3")])],"isStart":false});Q100=makeQuery(id+"F2.imprint","IMPRINT",FACE,{"disambiguationData":[TD([[makeQuery(id+"F2.imprint","IMPRINT",EDGE,{"derivedFrom":subQ5}),-1.0]])]});}
            var Q101;
            {var subQ5=makeQuery(id+"F1.opExtrude","CAP_EDGE",EDGE,{"disambiguationData":[OSD([sQuery(id+"F0.wireOp",EDGE,"E22.4.3")])],"isStart":false});Q101=makeQuery(id+"F2.imprint","IMPRINT",FACE,{"disambiguationData":[TD([[makeQuery(id+"F2.imprint","IMPRINT",EDGE,{"derivedFrom":subQ5}),-1.0]])]});}
            var Q102;
            {var subQ5=makeQuery(id+"F1.opExtrude","CAP_EDGE",EDGE,{"disambiguationData":[OSD([sQuery(id+"F0.wireOp",EDGE,"E22.5.3")])],"isStart":false});Q102=makeQuery(id+"F2.imprint","IMPRINT",FACE,{"disambiguationData":[TD([[makeQuery(id+"F2.imprint","IMPRINT",EDGE,{"derivedFrom":subQ5}),-1.0]])]});}
            var Q103;
            {var subQ5=makeQuery(id+"F1.opExtrude","CAP_EDGE",EDGE,{"disambiguationData":[OSD([sQuery(id+"F0.wireOp",EDGE,"E22.6.3")])],"isStart":false});Q103=makeQuery(id+"F2.imprint","IMPRINT",FACE,{"disambiguationData":[TD([[makeQuery(id+"F2.imprint","IMPRINT",EDGE,{"derivedFrom":subQ5}),-1.0]])]});}
            var Q104;
            {var subQ5=makeQuery(id+"F1.opExtrude","CAP_EDGE",EDGE,{"disambiguationData":[OSD([sQuery(id+"F0.wireOp",EDGE,"E22.7.3")])],"isStart":false});Q104=makeQuery(id+"F2.imprint","IMPRINT",FACE,{"disambiguationData":[TD([[makeQuery(id+"F2.imprint","IMPRINT",EDGE,{"derivedFrom":subQ5}),-1.0]])]});}
            var Q105;
            {var subQ5=makeQuery(id+"F1.opExtrude","CAP_EDGE",EDGE,{"disambiguationData":[OSD([sQuery(id+"F0.wireOp",EDGE,"E22.8.3")])],"isStart":false});Q105=makeQuery(id+"F2.imprint","IMPRINT",FACE,{"disambiguationData":[TD([[makeQuery(id+"F2.imprint","IMPRINT",EDGE,{"derivedFrom":subQ5}),-1.0]])]});}
            var Q106;
            {var subQ3=sQuery(id+"F2.wireOp",EDGE,"E24");var subQ5=makeQuery(id+"F1.opExtrude","CAP_EDGE",EDGE,{"disambiguationData":[OSD([sQuery(id+"F0.wireOp",EDGE,"E9.trimOffspring")])],"isStart":false});var subQ8=makeQuery(id+"F2.imprint","INTERSECT",VERTEX,{"derivedFrom":[subQ5,subQ3]});Q106=makeQuery(id+"F2.imprint","IMPRINT",FACE,{"disambiguationData":[TD([[makeQuery(id+"F2.imprint","IMPRINT",EDGE,{"disambiguationData":[TD([[subQ8,-1.0]])],"derivedFrom":subQ3}),-1.0]])]});}
            var Q107;
            {var subQ0=makeQuery(id+"F1.opExtrude","CAP_EDGE",EDGE,{"disambiguationData":[OSD([sQuery(id+"F0.wireOp",EDGE,"E3.0.startCap")])],"isStart":false});Q107=makeQuery(id+"F2.imprint","IMPRINT",FACE,{"disambiguationData":[TD([[makeQuery(id+"F2.imprint","IMPRINT",EDGE,{"derivedFrom":subQ0}),1.0]])]});}
            var Q108;
            {var subQ5=makeQuery(id+"F1.opExtrude","CAP_EDGE",EDGE,{"disambiguationData":[OSD([sQuery(id+"F0.wireOp",EDGE,"E3.0.startCap")])],"isStart":false});Q108=makeQuery(id+"F2.imprint","IMPRINT",FACE,{"disambiguationData":[TD([[makeQuery(id+"F2.imprint","IMPRINT",EDGE,{"derivedFrom":subQ5}),-1.0]])]});}
            var Q109;
            {var subQ0=makeQuery(id+"F1.opExtrude","CAP_EDGE",EDGE,{"disambiguationData":[OSD([sQuery(id+"F0.wireOp",EDGE,"E2.0.right")])],"isStart":false});var subQ4=sQuery(id+"F2.wireOp",EDGE,"E24");var subQ5=makeQuery(id+"F2.imprint","INTERSECT",VERTEX,{"derivedFrom":[subQ0,subQ4]});Q109=makeQuery(id+"F2.imprint","IMPRINT",FACE,{"disambiguationData":[TD([[makeQuery(id+"F2.imprint","IMPRINT",EDGE,{"disambiguationData":[TD([[subQ5,-1.0]])],"derivedFrom":subQ4}),-1.0]])]});}
            var Q110;
            {var subQ5=makeQuery(id+"F1.opExtrude","CAP_EDGE",EDGE,{"disambiguationData":[OSD([sQuery(id+"F0.wireOp",EDGE,"E22.15.1")])],"isStart":false});Q110=makeQuery(id+"F2.imprint","IMPRINT",FACE,{"disambiguationData":[TD([[makeQuery(id+"F2.imprint","IMPRINT",EDGE,{"derivedFrom":subQ5}),-1.0]])]});}
            var Q111;
            {var subQ3=sQuery(id+"F2.wireOp",EDGE,"E24");var subQ5=makeQuery(id+"F1.opExtrude","CAP_EDGE",EDGE,{"disambiguationData":[OSD([sQuery(id+"F0.wireOp",EDGE,"E11.trimOffspring")])],"isStart":false});var subQ8=makeQuery(id+"F2.imprint","INTERSECT",VERTEX,{"derivedFrom":[subQ5,subQ3]});Q111=makeQuery(id+"F2.imprint","IMPRINT",FACE,{"disambiguationData":[TD([[makeQuery(id+"F2.imprint","IMPRINT",EDGE,{"disambiguationData":[TD([[subQ8,-1.0]])],"derivedFrom":subQ3}),-1.0]])]});}
            var Q112;
            {var subQ5=makeQuery(id+"F1.opExtrude","CAP_EDGE",EDGE,{"disambiguationData":[OSD([sQuery(id+"F0.wireOp",EDGE,"E22.14.1")])],"isStart":false});Q112=makeQuery(id+"F2.imprint","IMPRINT",FACE,{"disambiguationData":[TD([[makeQuery(id+"F2.imprint","IMPRINT",EDGE,{"derivedFrom":subQ5}),-1.0]])]});}
            var Q113;
            {var subQ4=sQuery(id+"F2.wireOp",EDGE,"E24");var subQ5=makeQuery(id+"F1.opExtrude","CAP_EDGE",EDGE,{"disambiguationData":[OSD([sQuery(id+"F0.wireOp",EDGE,"E21.7.2")])],"isStart":false});var subQ6=makeQuery(id+"F2.imprint","INTERSECT",VERTEX,{"derivedFrom":[subQ5,subQ4]});Q113=makeQuery(id+"F2.imprint","IMPRINT",FACE,{"disambiguationData":[TD([[makeQuery(id+"F2.imprint","IMPRINT",EDGE,{"disambiguationData":[TD([[subQ6,-1.0]])],"derivedFrom":subQ4}),-1.0]])]});}
            var Q114;
            {var subQ5=makeQuery(id+"F1.opExtrude","CAP_EDGE",EDGE,{"disambiguationData":[OSD([sQuery(id+"F0.wireOp",EDGE,"E22.12.1")])],"isStart":false});Q114=makeQuery(id+"F2.imprint","IMPRINT",FACE,{"disambiguationData":[TD([[makeQuery(id+"F2.imprint","IMPRINT",EDGE,{"derivedFrom":subQ5}),-1.0]])]});}
            var Q115;
            {var subQ4=sQuery(id+"F2.wireOp",EDGE,"E24");var subQ6=makeQuery(id+"F1.opExtrude","CAP_EDGE",EDGE,{"disambiguationData":[OSD([sQuery(id+"F0.wireOp",EDGE,"E21.6.2")])],"isStart":false});var subQ7=makeQuery(id+"F2.imprint","INTERSECT",VERTEX,{"derivedFrom":[subQ6,subQ4]});Q115=makeQuery(id+"F2.imprint","IMPRINT",FACE,{"disambiguationData":[TD([[makeQuery(id+"F2.imprint","IMPRINT",EDGE,{"disambiguationData":[TD([[subQ7,-1.0]])],"derivedFrom":subQ4}),-1.0]])]});}
            var Q116;
            {var subQ5=makeQuery(id+"F1.opExtrude","CAP_EDGE",EDGE,{"disambiguationData":[OSD([sQuery(id+"F0.wireOp",EDGE,"E22.11.1")])],"isStart":false});Q116=makeQuery(id+"F2.imprint","IMPRINT",FACE,{"disambiguationData":[TD([[makeQuery(id+"F2.imprint","IMPRINT",EDGE,{"derivedFrom":subQ5}),-1.0]])]});}
            var Q117;
            {var subQ0=makeQuery(id+"F1.opExtrude","CAP_EDGE",EDGE,{"disambiguationData":[OSD([sQuery(id+"F0.wireOp",EDGE,"E14.trimOffspring")])],"isStart":false});var subQ6=sQuery(id+"F2.wireOp",EDGE,"E24");var subQ8=makeQuery(id+"F2.imprint","INTERSECT",VERTEX,{"derivedFrom":[subQ0,subQ6]});Q117=makeQuery(id+"F2.imprint","IMPRINT",FACE,{"disambiguationData":[TD([[makeQuery(id+"F2.imprint","IMPRINT",EDGE,{"disambiguationData":[TD([[subQ8,-1.0]])],"derivedFrom":subQ6}),-1.0]])]});}
            var Q118;
            {var subQ0=makeQuery(id+"F1.opExtrude","CAP_EDGE",EDGE,{"disambiguationData":[OSD([sQuery(id+"F0.wireOp",EDGE,"E22.10.1")])],"isStart":false});Q118=makeQuery(id+"F2.imprint","IMPRINT",FACE,{"disambiguationData":[TD([[makeQuery(id+"F2.imprint","IMPRINT",EDGE,{"derivedFrom":subQ0}),1.0]])]});}
            var Q119;
            {var subQ5=makeQuery(id+"F1.opExtrude","CAP_EDGE",EDGE,{"disambiguationData":[OSD([sQuery(id+"F0.wireOp",EDGE,"E22.10.1")])],"isStart":false});Q119=makeQuery(id+"F2.imprint","IMPRINT",FACE,{"disambiguationData":[TD([[makeQuery(id+"F2.imprint","IMPRINT",EDGE,{"derivedFrom":subQ5}),-1.0]])]});}
            var Q120;
            {var subQ0=makeQuery(id+"F1.opExtrude","CAP_EDGE",EDGE,{"disambiguationData":[OSD([sQuery(id+"F0.wireOp",EDGE,"E21.5.2")])],"isStart":false});var subQ6=sQuery(id+"F2.wireOp",EDGE,"E24");var subQ7=makeQuery(id+"F2.imprint","INTERSECT",VERTEX,{"derivedFrom":[subQ0,subQ6]});Q120=makeQuery(id+"F2.imprint","IMPRINT",FACE,{"disambiguationData":[TD([[makeQuery(id+"F2.imprint","IMPRINT",EDGE,{"disambiguationData":[TD([[subQ7,-1.0]])],"derivedFrom":subQ6}),-1.0]])]});}
            var Q121;
            {var subQ0=makeQuery(id+"F1.opExtrude","CAP_EDGE",EDGE,{"disambiguationData":[OSD([sQuery(id+"F0.wireOp",EDGE,"E22.9.1")])],"isStart":false});Q121=makeQuery(id+"F2.imprint","IMPRINT",FACE,{"disambiguationData":[TD([[makeQuery(id+"F2.imprint","IMPRINT",EDGE,{"derivedFrom":subQ0}),1.0]])]});}
            var Q122;
            {var subQ5=makeQuery(id+"F1.opExtrude","CAP_EDGE",EDGE,{"disambiguationData":[OSD([sQuery(id+"F0.wireOp",EDGE,"E22.9.1")])],"isStart":false});Q122=makeQuery(id+"F2.imprint","IMPRINT",FACE,{"disambiguationData":[TD([[makeQuery(id+"F2.imprint","IMPRINT",EDGE,{"derivedFrom":subQ5}),-1.0]])]});}
            var Q123;
            {var subQ3=sQuery(id+"F2.wireOp",EDGE,"E24");var subQ6=makeQuery(id+"F1.opExtrude","CAP_EDGE",EDGE,{"disambiguationData":[OSD([sQuery(id+"F0.wireOp",EDGE,"E16.trimOffspring")])],"isStart":false});var subQ8=makeQuery(id+"F2.imprint","INTERSECT",VERTEX,{"derivedFrom":[subQ6,subQ3]});Q123=makeQuery(id+"F2.imprint","IMPRINT",FACE,{"disambiguationData":[TD([[makeQuery(id+"F2.imprint","IMPRINT",EDGE,{"disambiguationData":[TD([[subQ8,-1.0]])],"derivedFrom":subQ3}),-1.0]])]});}
            var Q124;
            {var subQ0=makeQuery(id+"F1.opExtrude","CAP_EDGE",EDGE,{"disambiguationData":[OSD([sQuery(id+"F0.wireOp",EDGE,"E22.8.1")])],"isStart":false});Q124=makeQuery(id+"F2.imprint","IMPRINT",FACE,{"disambiguationData":[TD([[makeQuery(id+"F2.imprint","IMPRINT",EDGE,{"derivedFrom":subQ0}),1.0]])]});}
            var Q125;
            {var subQ5=makeQuery(id+"F1.opExtrude","CAP_EDGE",EDGE,{"disambiguationData":[OSD([sQuery(id+"F0.wireOp",EDGE,"E22.8.1")])],"isStart":false});Q125=makeQuery(id+"F2.imprint","IMPRINT",FACE,{"disambiguationData":[TD([[makeQuery(id+"F2.imprint","IMPRINT",EDGE,{"derivedFrom":subQ5}),-1.0]])]});}
            var Q126;
            {var subQ0=makeQuery(id+"F1.opExtrude","CAP_EDGE",EDGE,{"disambiguationData":[OSD([sQuery(id+"F0.wireOp",EDGE,"E21.4.2")])],"isStart":false});var subQ4=sQuery(id+"F2.wireOp",EDGE,"E24");var subQ5=makeQuery(id+"F2.imprint","INTERSECT",VERTEX,{"derivedFrom":[subQ0,subQ4]});Q126=makeQuery(id+"F2.imprint","IMPRINT",FACE,{"disambiguationData":[TD([[makeQuery(id+"F2.imprint","IMPRINT",EDGE,{"disambiguationData":[TD([[subQ5,-1.0]])],"derivedFrom":subQ4}),-1.0]])]});}
            var Q127;
            {var subQ10=makeQuery(id+"F1.opExtrude","CAP_EDGE",EDGE,{"disambiguationData":[OSD([sQuery(id+"F0.wireOp",EDGE,"E22.7.1")])],"isStart":false});Q127=makeQuery(id+"F2.imprint","IMPRINT",FACE,{"disambiguationData":[TD([[makeQuery(id+"F2.imprint","IMPRINT",EDGE,{"derivedFrom":subQ10}),1.0]])]});}
            var Q128;
            {var subQ5=makeQuery(id+"F1.opExtrude","CAP_EDGE",EDGE,{"disambiguationData":[OSD([sQuery(id+"F0.wireOp",EDGE,"E22.7.1")])],"isStart":false});Q128=makeQuery(id+"F2.imprint","IMPRINT",FACE,{"disambiguationData":[TD([[makeQuery(id+"F2.imprint","IMPRINT",EDGE,{"derivedFrom":subQ5}),-1.0]])]});}
            var Q129;
            {var subQ0=makeQuery(id+"F1.opExtrude","CAP_EDGE",EDGE,{"disambiguationData":[OSD([sQuery(id+"F0.wireOp",EDGE,"E18.trimOffspring")])],"isStart":false});var subQ6=sQuery(id+"F2.wireOp",EDGE,"E24");var subQ8=makeQuery(id+"F2.imprint","INTERSECT",VERTEX,{"derivedFrom":[subQ0,subQ6]});Q129=makeQuery(id+"F2.imprint","IMPRINT",FACE,{"disambiguationData":[TD([[makeQuery(id+"F2.imprint","IMPRINT",EDGE,{"disambiguationData":[TD([[subQ8,-1.0]])],"derivedFrom":subQ6}),-1.0]])]});}
            var Q130;
            {var subQ5=makeQuery(id+"F1.opExtrude","CAP_EDGE",EDGE,{"disambiguationData":[OSD([sQuery(id+"F0.wireOp",EDGE,"E22.6.1")])],"isStart":false});Q130=makeQuery(id+"F2.imprint","IMPRINT",FACE,{"disambiguationData":[TD([[makeQuery(id+"F2.imprint","IMPRINT",EDGE,{"derivedFrom":subQ5}),-1.0]])]});}
            var Q131;
            {var subQ0=makeQuery(id+"F1.opExtrude","CAP_EDGE",EDGE,{"disambiguationData":[OSD([sQuery(id+"F0.wireOp",EDGE,"E21.3.2")])],"isStart":false});var subQ6=sQuery(id+"F2.wireOp",EDGE,"E24");var subQ8=makeQuery(id+"F2.imprint","INTERSECT",VERTEX,{"derivedFrom":[subQ0,subQ6]});Q131=makeQuery(id+"F2.imprint","IMPRINT",FACE,{"disambiguationData":[TD([[makeQuery(id+"F2.imprint","IMPRINT",EDGE,{"disambiguationData":[TD([[subQ8,-1.0]])],"derivedFrom":subQ6}),-1.0]])]});}
            var Q132;
            {var subQ0=makeQuery(id+"F1.opExtrude","CAP_EDGE",EDGE,{"disambiguationData":[OSD([sQuery(id+"F0.wireOp",EDGE,"E22.5.1")])],"isStart":false});Q132=makeQuery(id+"F2.imprint","IMPRINT",FACE,{"disambiguationData":[TD([[makeQuery(id+"F2.imprint","IMPRINT",EDGE,{"derivedFrom":subQ0}),1.0]])]});}
            var Q133;
            {var subQ5=makeQuery(id+"F1.opExtrude","CAP_EDGE",EDGE,{"disambiguationData":[OSD([sQuery(id+"F0.wireOp",EDGE,"E22.5.1")])],"isStart":false});Q133=makeQuery(id+"F2.imprint","IMPRINT",FACE,{"disambiguationData":[TD([[makeQuery(id+"F2.imprint","IMPRINT",EDGE,{"derivedFrom":subQ5}),-1.0]])]});}
            var Q134;
            {var subQ0=makeQuery(id+"F1.opExtrude","CAP_EDGE",EDGE,{"disambiguationData":[OSD([sQuery(id+"F0.wireOp",EDGE,"E6.trimOffspring")])],"isStart":false});var subQ6=sQuery(id+"F2.wireOp",EDGE,"E24");var subQ7=makeQuery(id+"F2.imprint","INTERSECT",VERTEX,{"derivedFrom":[subQ0,subQ6]});Q134=makeQuery(id+"F2.imprint","IMPRINT",FACE,{"disambiguationData":[TD([[makeQuery(id+"F2.imprint","IMPRINT",EDGE,{"disambiguationData":[TD([[subQ7,-1.0]])],"derivedFrom":subQ6}),-1.0]])]});}
            var Q135;
            {var subQ0=makeQuery(id+"F1.opExtrude","CAP_EDGE",EDGE,{"disambiguationData":[OSD([sQuery(id+"F0.wireOp",EDGE,"E22.4.1")])],"isStart":false});Q135=makeQuery(id+"F2.imprint","IMPRINT",FACE,{"disambiguationData":[TD([[makeQuery(id+"F2.imprint","IMPRINT",EDGE,{"derivedFrom":subQ0}),1.0]])]});}
            var Q136;
            {var subQ5=makeQuery(id+"F1.opExtrude","CAP_EDGE",EDGE,{"disambiguationData":[OSD([sQuery(id+"F0.wireOp",EDGE,"E22.4.1")])],"isStart":false});Q136=makeQuery(id+"F2.imprint","IMPRINT",FACE,{"disambiguationData":[TD([[makeQuery(id+"F2.imprint","IMPRINT",EDGE,{"derivedFrom":subQ5}),-1.0]])]});}
            var Q137;
            {var subQ0=makeQuery(id+"F1.opExtrude","CAP_EDGE",EDGE,{"disambiguationData":[OSD([sQuery(id+"F0.wireOp",EDGE,"E21.2.2")])],"isStart":false});var subQ6=sQuery(id+"F2.wireOp",EDGE,"E24");var subQ8=makeQuery(id+"F2.imprint","INTERSECT",VERTEX,{"derivedFrom":[subQ0,subQ6]});Q137=makeQuery(id+"F2.imprint","IMPRINT",FACE,{"disambiguationData":[TD([[makeQuery(id+"F2.imprint","IMPRINT",EDGE,{"disambiguationData":[TD([[subQ8,-1.0]])],"derivedFrom":subQ6}),-1.0]])]});}
            var Q138;
            {var subQ0=makeQuery(id+"F1.opExtrude","CAP_EDGE",EDGE,{"disambiguationData":[OSD([sQuery(id+"F0.wireOp",EDGE,"E22.3.1")])],"isStart":false});Q138=makeQuery(id+"F2.imprint","IMPRINT",FACE,{"disambiguationData":[TD([[makeQuery(id+"F2.imprint","IMPRINT",EDGE,{"derivedFrom":subQ0}),1.0]])]});}
            var Q139;
            {var subQ5=makeQuery(id+"F1.opExtrude","CAP_EDGE",EDGE,{"disambiguationData":[OSD([sQuery(id+"F0.wireOp",EDGE,"E22.3.1")])],"isStart":false});Q139=makeQuery(id+"F2.imprint","IMPRINT",FACE,{"disambiguationData":[TD([[makeQuery(id+"F2.imprint","IMPRINT",EDGE,{"derivedFrom":subQ5}),-1.0]])]});}
            var Q140;
            {var subQ0=makeQuery(id+"F1.opExtrude","CAP_EDGE",EDGE,{"disambiguationData":[OSD([sQuery(id+"F0.wireOp",EDGE,"E7.trimOffspring")])],"isStart":false});var subQ4=sQuery(id+"F2.wireOp",EDGE,"E24");var subQ5=makeQuery(id+"F2.imprint","INTERSECT",VERTEX,{"derivedFrom":[subQ0,subQ4]});Q140=makeQuery(id+"F2.imprint","IMPRINT",FACE,{"disambiguationData":[TD([[makeQuery(id+"F2.imprint","IMPRINT",EDGE,{"disambiguationData":[TD([[subQ5,-1.0]])],"derivedFrom":subQ4}),-1.0]])]});}
            var Q141;
            {var subQ13=makeQuery(id+"F1.opExtrude","CAP_EDGE",EDGE,{"disambiguationData":[OSD([sQuery(id+"F0.wireOp",EDGE,"E22.2.1")])],"isStart":false});Q141=makeQuery(id+"F2.imprint","IMPRINT",FACE,{"disambiguationData":[TD([[makeQuery(id+"F2.imprint","IMPRINT",EDGE,{"derivedFrom":subQ13}),1.0]])]});}
            var Q142;
            {var subQ5=makeQuery(id+"F1.opExtrude","CAP_EDGE",EDGE,{"disambiguationData":[OSD([sQuery(id+"F0.wireOp",EDGE,"E22.2.1")])],"isStart":false});Q142=makeQuery(id+"F2.imprint","IMPRINT",FACE,{"disambiguationData":[TD([[makeQuery(id+"F2.imprint","IMPRINT",EDGE,{"derivedFrom":subQ5}),-1.0]])]});}
            var Q143;
            {var subQ4=sQuery(id+"F2.wireOp",EDGE,"E24");var subQ6=makeQuery(id+"F1.opExtrude","CAP_EDGE",EDGE,{"disambiguationData":[OSD([sQuery(id+"F0.wireOp",EDGE,"E21.1.2")])],"isStart":false});var subQ8=makeQuery(id+"F2.imprint","INTERSECT",VERTEX,{"derivedFrom":[subQ6,subQ4]});Q143=makeQuery(id+"F2.imprint","IMPRINT",FACE,{"disambiguationData":[TD([[makeQuery(id+"F2.imprint","IMPRINT",EDGE,{"disambiguationData":[TD([[subQ8,-1.0]])],"derivedFrom":subQ4}),-1.0]])]});}
            var Q144;
            {var subQ0=makeQuery(id+"F1.opExtrude","CAP_EDGE",EDGE,{"disambiguationData":[OSD([sQuery(id+"F0.wireOp",EDGE,"E22.1.1")])],"isStart":false});Q144=makeQuery(id+"F2.imprint","IMPRINT",FACE,{"disambiguationData":[TD([[makeQuery(id+"F2.imprint","IMPRINT",EDGE,{"derivedFrom":subQ0}),1.0]])]});}
            var Q145;
            {var subQ5=makeQuery(id+"F1.opExtrude","CAP_EDGE",EDGE,{"disambiguationData":[OSD([sQuery(id+"F0.wireOp",EDGE,"E22.1.1")])],"isStart":false});Q145=makeQuery(id+"F2.imprint","IMPRINT",FACE,{"disambiguationData":[TD([[makeQuery(id+"F2.imprint","IMPRINT",EDGE,{"derivedFrom":subQ5}),-1.0]])]});}
            var Q146;
            {var subQ10=makeQuery(id+"F1.opExtrude","CAP_EDGE",EDGE,{"disambiguationData":[OSD([sQuery(id+"F0.wireOp",EDGE,"E22.14.1")])],"isStart":false});Q146=makeQuery(id+"F2.imprint","IMPRINT",FACE,{"disambiguationData":[TD([[makeQuery(id+"F2.imprint","IMPRINT",EDGE,{"derivedFrom":subQ10}),1.0]])]});}
            var Q147;
            {var subQ0=makeQuery(id+"F1.opExtrude","CAP_EDGE",EDGE,{"disambiguationData":[OSD([sQuery(id+"F0.wireOp",EDGE,"E22.15.1")])],"isStart":false});Q147=makeQuery(id+"F2.imprint","IMPRINT",FACE,{"disambiguationData":[TD([[makeQuery(id+"F2.imprint","IMPRINT",EDGE,{"derivedFrom":subQ0}),1.0]])]});}
            var Q148;
            {var subQ0=makeQuery(id+"F1.opExtrude","CAP_EDGE",EDGE,{"disambiguationData":[OSD([sQuery(id+"F0.wireOp",EDGE,"E22.6.1")])],"isStart":false});Q148=makeQuery(id+"F2.imprint","IMPRINT",FACE,{"disambiguationData":[TD([[makeQuery(id+"F2.imprint","IMPRINT",EDGE,{"derivedFrom":subQ0}),1.0]])]});}
            var Q149;
            {var subQ6=makeQuery(id+"F1.opExtrude","CAP_EDGE",EDGE,{"disambiguationData":[OSD([sQuery(id+"F0.wireOp",EDGE,"E22.12.1")])],"isStart":false});Q149=makeQuery(id+"F2.imprint","IMPRINT",FACE,{"disambiguationData":[TD([[makeQuery(id+"F2.imprint","IMPRINT",EDGE,{"derivedFrom":subQ6}),1.0]])]});}
            var Q150;
            {var subQ0=makeQuery(id+"F1.opExtrude","CAP_EDGE",EDGE,{"disambiguationData":[OSD([sQuery(id+"F0.wireOp",EDGE,"E22.11.1")])],"isStart":false});Q150=makeQuery(id+"F2.imprint","IMPRINT",FACE,{"disambiguationData":[TD([[makeQuery(id+"F2.imprint","IMPRINT",EDGE,{"derivedFrom":subQ0}),1.0]])]});}
            var Q151;
            {var subQ0=makeQuery(id+"F1.opExtrude","CAP_EDGE",EDGE,{"disambiguationData":[OSD([sQuery(id+"F0.wireOp",EDGE,"E10.trimOffspring")])],"isStart":false});var subQ3=sQuery(id+"F2.wireOp",EDGE,"E24");var subQ4=makeQuery(id+"F2.imprint","INTERSECT",VERTEX,{"derivedFrom":[subQ0,subQ3]});Q151=makeQuery(id+"F2.imprint","IMPRINT",FACE,{"disambiguationData":[TD([[makeQuery(id+"F2.imprint","IMPRINT",EDGE,{"disambiguationData":[TD([[subQ4,1.0]])],"derivedFrom":subQ3}),-1.0]])]});}
            var Q152;
            {var subQ5=makeQuery(id+"F1.opExtrude","CAP_EDGE",EDGE,{"disambiguationData":[OSD([sQuery(id+"F0.wireOp",EDGE,"E22.13.1")])],"isStart":false});Q152=makeQuery(id+"F2.imprint","IMPRINT",FACE,{"disambiguationData":[TD([[makeQuery(id+"F2.imprint","IMPRINT",EDGE,{"derivedFrom":subQ5}),1.0]])]});}
            var Q153;
            {var subQ5=makeQuery(id+"F1.opExtrude","CAP_EDGE",EDGE,{"disambiguationData":[OSD([sQuery(id+"F0.wireOp",EDGE,"E22.13.1")])],"isStart":false});Q153=makeQuery(id+"F2.imprint","IMPRINT",FACE,{"disambiguationData":[TD([[makeQuery(id+"F2.imprint","IMPRINT",EDGE,{"derivedFrom":subQ5}),-1.0]])]});}
            var Q154;
            Q154=makeQuery(id+"F2.imprint","IMPRINT",FACE,{"disambiguationData":[TD([[makeQuery(id+"F2.imprint","IMPRINT",EDGE,{"derivedFrom":sQuery(id+"F2.wireOp",EDGE,"E26")}),-1.0]])]});
            extrude(context, id + "F3", {"entities" : qUnion([Q0, Q1, Q2, Q3, Q4, Q5, Q6, Q7, Q8, Q9, Q10, Q11, Q12, Q13, Q14, Q15, Q16, Q17, Q18, Q19, Q20, Q21, Q22, Q23, Q24, Q25, Q26, Q27, Q28, Q29, Q30, Q31, Q32, Q33, Q34, Q35, Q36, Q37, Q38, Q39, Q40, Q41, Q42, Q43, Q44, Q45, Q46, Q47, Q48, Q49, Q50, Q51, Q52, Q53, Q54, Q55, Q56, Q57, Q58, Q59, Q60, Q61, Q62, Q63, Q64, Q65, Q66, Q67, Q68, Q69, Q70, Q71, Q72, Q73, Q74, Q75, Q76, Q77, Q78, Q79, Q80, Q81, Q82, Q83, Q84, Q85, Q86, Q87, Q88, Q89, Q90, Q91, Q92, Q93, Q94, Q95, Q96, Q97, Q98, Q99, Q100, Q101, Q102, Q103, Q104, Q105, Q106, Q107, Q108, Q109, Q110, Q111, Q112, Q113, Q114, Q115, Q116, Q117, Q118, Q119, Q120, Q121, Q122, Q123, Q124, Q125, Q126, Q127, Q128, Q129, Q130, Q131, Q132, Q133, Q134, Q135, Q136, Q137, Q138, Q139, Q140, Q141, Q142, Q143, Q144, Q145, Q146, Q147, Q148, Q149, Q150, Q151, Q152, Q153, Q154]), "operationType" : NewBodyOperationType.ADD, "depth" : 4 * mm});
        }
    });
